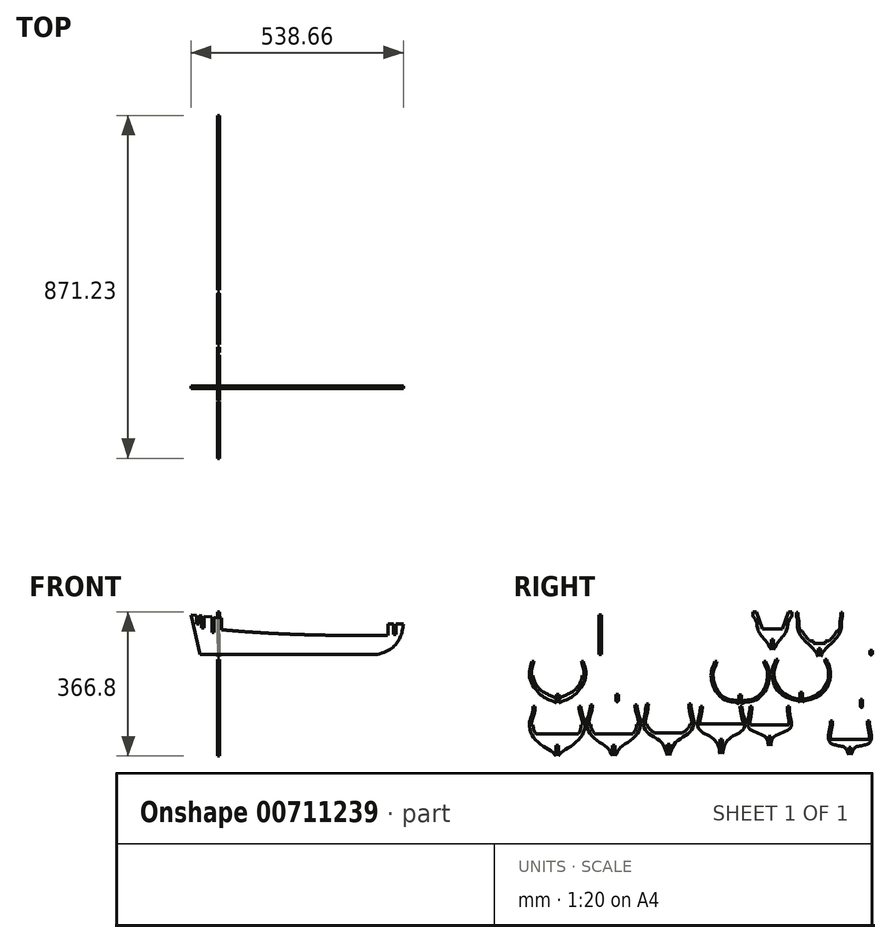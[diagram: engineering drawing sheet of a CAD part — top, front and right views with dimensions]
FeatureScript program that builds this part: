
annotation { "Feature Type Name" : "Feature", "Feature Type Description" : "" }
export const myFeature = defineFeature(function(context is Context, id is Id, definition is map)
    precondition{}
    {
        {
            var Q0;
            Q0=qCreatedBy(makeId("Right.planeOp"),FACE);
            var sketch = newSketch(context, id + "F0", { "sketchPlane" : qUnion([Q0]), "disableImprinting" : false});
            skLineSegment(sketch, "E0", {"start": v(434.23, 36.76) * mm, "end": v(434.23, -63.24) * mm, "construction": true});
            skLineSegment(sketch, "E1", {"start": v(474.96, 36.76) * mm, "end": v(484.23, 36.76) * mm, "construction": true});
            skLineSegment(sketch, "E2", {"start": v(484.23, 36.76) * mm, "end": v(484.23, 26.76) * mm});
            skFitSpline(sketch, "E3", {"points": [v(484.23, 26.76) * mm, v(475.06, 12.03) * mm, v(469.54, -13) * mm, v(437.23, -60.52) * mm], "startDerivative": vector(-48.23, -63.75) * mm, "endDerivative": vector(-86.6, -185.01) * mm});
            skLineSegment(sketch, "E4", {"start": v(431.23, -33.48) * mm, "end": v(437.23, -33.48) * mm});
            skLineSegment(sketch, "E5", {"start": v(437.23, -33.48) * mm, "end": v(437.23, -60.52) * mm});
            skLineSegment(sketch, "E6.MirrorCS", {"start": v(437.23, -33.48) * mm, "end": v(431.23, -33.48) * mm});
            skFitSpline(sketch, "E7.MirrorCS", {"points": [v(384.23, 26.76) * mm, v(393.4, 12.03) * mm, v(398.93, -13) * mm, v(431.23, -60.52) * mm], "startDerivative": vector(48.23, -63.75) * mm, "endDerivative": vector(86.6, -185.01) * mm});
            skLineSegment(sketch, "E8.MirrorCS", {"start": v(393.5, 36.76) * mm, "end": v(384.23, 36.76) * mm, "construction": true});
            skLineSegment(sketch, "E9.MirrorCS", {"start": v(384.23, 36.76) * mm, "end": v(384.23, 26.76) * mm});
            skLineSegment(sketch, "E10.MirrorCS", {"start": v(431.23, -33.48) * mm, "end": v(431.23, -60.52) * mm});
            skLineSegment(sketch, "E11", {"start": v(384.23, 36.76) * mm, "end": v(393.5, 36.76) * mm});
            skLineSegment(sketch, "E12", {"start": v(434.23, -6.45) * mm, "end": v(459.23, -6.45) * mm});
            skLineSegment(sketch, "E13", {"start": v(459.23, -6.45) * mm, "end": v(474.96, 36.76) * mm});
            skLineSegment(sketch, "E14.MirrorCS", {"start": v(409.23, -6.45) * mm, "end": v(393.5, 36.76) * mm});
            skLineSegment(sketch, "E15.MirrorCS", {"start": v(434.23, -6.45) * mm, "end": v(409.23, -6.45) * mm});
            skPoint(sketch, "E16.orphan", {"position": v(434.23, 36.76) * mm});
            skLineSegment(sketch, "E17.trimOffspring", {"start": v(474.96, 36.76) * mm, "end": v(484.23, 36.76) * mm});
            skLineSegment(sketch, "E18", {"start": v(553.88, 36.76) * mm, "end": v(553.88, -78.24) * mm, "construction": true});
            skLineSegment(sketch, "E19", {"start": v(553.88, -56.43) * mm, "end": v(556.88, -56.43) * mm});
            skLineSegment(sketch, "E20", {"start": v(556.88, -56.43) * mm, "end": v(556.88, -76.43) * mm});
            skLineSegment(sketch, "E21", {"start": v(553.88, -43.08) * mm, "end": v(568.88, -43.08) * mm});
            skLineSegment(sketch, "E22", {"start": v(568.88, -43.08) * mm, "end": v(568.88, -37.08) * mm});
            skLineSegment(sketch, "E23", {"start": v(568.88, -37.08) * mm, "end": v(577.88, -37.08) * mm});
            skFitSpline(sketch, "E24", {"points": [v(577.88, -37.08) * mm, v(597.74, -12.04) * mm], "startDerivative": vector(24.58, 23.27) * mm, "endDerivative": vector(15.3, 31.89) * mm});
            skLineSegment(sketch, "E25", {"start": v(597.74, -12.04) * mm, "end": v(602.74, -12.04) * mm});
            skFitSpline(sketch, "E26", {"points": [v(602.74, -12.04) * mm, v(605.55, -2.16) * mm, v(606.03, 9.62) * mm, v(608.04, 23.19) * mm], "startDerivative": vector(9.73, 30.2) * mm, "endDerivative": vector(10.82, 49.21) * mm});
            skLineSegment(sketch, "E27", {"start": v(608.04, 23.19) * mm, "end": v(608.04, 35.69) * mm});
            skLineSegment(sketch, "E28", {"start": v(608.04, 35.69) * mm, "end": v(612.04, 35.69) * mm});
            skLineSegment(sketch, "E29", {"start": v(612.04, 35.69) * mm, "end": v(612.04, 23.19) * mm});
            skFitSpline(sketch, "E30", {"points": [v(612.04, 23.19) * mm, v(610.08, 13.13) * mm, v(606.58, -13.87) * mm, v(581.84, -45.86) * mm, v(556.88, -76.43) * mm], "startDerivative": vector(-26.95, -57.35) * mm, "endDerivative": vector(-67.73, -147.25) * mm});
            skLineSegment(sketch, "E31.MirrorCS", {"start": v(510, -12.04) * mm, "end": v(505, -12.04) * mm});
            skLineSegment(sketch, "E32.MirrorCS", {"start": v(538.88, -43.08) * mm, "end": v(538.88, -37.08) * mm});
            skLineSegment(sketch, "E33.MirrorCS", {"start": v(499.71, 35.69) * mm, "end": v(495.71, 35.69) * mm});
            skLineSegment(sketch, "E34.MirrorCS", {"start": v(538.88, -37.08) * mm, "end": v(529.88, -37.08) * mm});
            skLineSegment(sketch, "E35.MirrorCS", {"start": v(553.88, -56.43) * mm, "end": v(550.88, -56.43) * mm});
            skLineSegment(sketch, "E36.MirrorCS", {"start": v(499.71, 23.19) * mm, "end": v(499.71, 35.69) * mm});
            skLineSegment(sketch, "E37.MirrorCS", {"start": v(553.88, -43.08) * mm, "end": v(538.88, -43.08) * mm});
            skFitSpline(sketch, "E38.MirrorCS", {"points": [v(529.88, -37.08) * mm, v(510, -12.04) * mm], "startDerivative": vector(-24.58, 23.27) * mm, "endDerivative": vector(-15.3, 31.89) * mm});
            skFitSpline(sketch, "E39.MirrorCS", {"points": [v(495.71, 23.19) * mm, v(497.67, 13.13) * mm, v(501.17, -13.87) * mm, v(525.9, -45.86) * mm, v(550.88, -76.43) * mm], "startDerivative": vector(26.95, -57.35) * mm, "endDerivative": vector(67.73, -147.25) * mm});
            skLineSegment(sketch, "E40.MirrorCS", {"start": v(495.71, 35.69) * mm, "end": v(495.71, 23.19) * mm});
            skFitSpline(sketch, "E41.MirrorCS", {"points": [v(505, -12.04) * mm, v(502.2, -2.16) * mm, v(501.73, 9.62) * mm, v(499.71, 23.19) * mm], "startDerivative": vector(-9.73, 30.2) * mm, "endDerivative": vector(-10.82, 49.21) * mm});
            skLineSegment(sketch, "E42.MirrorCS", {"start": v(550.88, -56.43) * mm, "end": v(550.88, -76.43) * mm});
            skLineSegment(sketch, "E43", {"start": v(631.29, -238.47) * mm, "end": v(631.29, -331.47) * mm, "construction": true});
            skLineSegment(sketch, "E44", {"start": v(631.29, -307.47) * mm, "end": v(634.29, -307.47) * mm});
            skLineSegment(sketch, "E45", {"start": v(634.29, -307.47) * mm, "end": v(634.29, -327.47) * mm});
            skLineSegment(sketch, "E46", {"start": v(631.29, -287.47) * mm, "end": v(680.29, -287.47) * mm});
            skFitSpline(sketch, "E47", {"points": [v(680.29, -287.47) * mm, v(676.8, -255.54) * mm, v(675.93, -240.32) * mm], "startDerivative": vector(6.96, 57.92) * mm, "endDerivative": vector(0.97, 34.08) * mm});
            skLineSegment(sketch, "E48", {"start": v(675.93, -240.32) * mm, "end": v(680.93, -240.32) * mm});
            skFitSpline(sketch, "E49.0", {"points": [v(685.26, -287.9) * mm, v(685.58, -285.19) * mm, v(685.74, -279.83) * mm, v(685.13, -273.43) * mm, v(684.4, -268.56) * mm, v(683.76, -265.07) * mm, v(683.1, -261.75) * mm, v(682.48, -258.64) * mm, v(682.02, -256.25) * mm, v(681.72, -254.48) * mm, v(681.46, -252.8) * mm, v(681.21, -250.8) * mm, v(681.02, -248.57) * mm, v(680.9, -246.45) * mm, v(680.85, -243.7) * mm, v(680.89, -241.67) * mm, v(680.93, -240.29) * mm]});
            skFitSpline(sketch, "E50", {"points": [v(685.28, -287.7) * mm, v(677.18, -298.82) * mm, v(646.16, -307.43) * mm, v(634.29, -327.47) * mm], "startDerivative": vector(-1.84, -29.1) * mm, "endDerivative": vector(-19.55, -69.03) * mm});
            skLineSegment(sketch, "E51.MirrorCS", {"start": v(631.29, -307.47) * mm, "end": v(628.29, -307.47) * mm});
            skLineSegment(sketch, "E52.MirrorCS", {"start": v(586.65, -240.32) * mm, "end": v(581.65, -240.32) * mm});
            skFitSpline(sketch, "E53.MirrorCS", {"points": [v(577.32, -287.9) * mm, v(577, -285.19) * mm, v(576.84, -279.83) * mm, v(577.44, -273.43) * mm, v(578.19, -268.56) * mm, v(578.82, -265.07) * mm, v(579.47, -261.75) * mm, v(580.1, -258.64) * mm, v(580.56, -256.25) * mm, v(580.86, -254.48) * mm, v(581.12, -252.8) * mm, v(581.36, -250.8) * mm, v(581.56, -248.57) * mm, v(581.67, -246.45) * mm, v(581.72, -243.7) * mm, v(581.69, -241.67) * mm, v(581.65, -240.29) * mm]});
            skLineSegment(sketch, "E54.MirrorCS", {"start": v(631.29, -287.47) * mm, "end": v(582.29, -287.47) * mm});
            skFitSpline(sketch, "E55.MirrorCS", {"points": [v(577.3, -287.7) * mm, v(585.4, -298.82) * mm, v(616.42, -307.43) * mm, v(628.29, -327.47) * mm], "startDerivative": vector(1.84, -29.1) * mm, "endDerivative": vector(19.55, -69.03) * mm});
            skLineSegment(sketch, "E56.MirrorCS", {"start": v(628.29, -307.47) * mm, "end": v(628.29, -327.47) * mm});
            skFitSpline(sketch, "E57.MirrorCS", {"points": [v(582.29, -287.47) * mm, v(585.78, -255.54) * mm, v(586.65, -240.32) * mm], "startDerivative": vector(-6.96, 57.92) * mm, "endDerivative": vector(-0.97, 34.08) * mm});
            skLineSegment(sketch, "E58", {"start": v(427.1, -199.94) * mm, "end": v(427.1, -292.94) * mm, "construction": true});
            skLineSegment(sketch, "E59", {"start": v(427.1, -280.2) * mm, "end": v(430.1, -280.2) * mm});
            skLineSegment(sketch, "E60", {"start": v(430.1, -280.2) * mm, "end": v(430.1, -303.67) * mm});
            skLineSegment(sketch, "E61", {"start": v(427.1, -250.2) * mm, "end": v(476.1, -250.2) * mm});
            skFitSpline(sketch, "E62", {"points": [v(476.1, -250.2) * mm, v(474.89, -230.87) * mm, v(471.92, -203.24) * mm], "startDerivative": vector(6.96, 57.92) * mm, "endDerivative": vector(0.97, 34.08) * mm});
            skLineSegment(sketch, "E63", {"start": v(471.92, -203.24) * mm, "end": v(476.92, -203.24) * mm});
            skFitSpline(sketch, "E64", {"points": [v(476.92, -203.24) * mm, v(480.45, -258.14) * mm, v(439.2, -280.1) * mm, v(430.1, -303.67) * mm], "startDerivative": vector(-10.38, -162.31) * mm, "endDerivative": vector(0, -73.72) * mm});
            skLineSegment(sketch, "E65.MirrorCS", {"start": v(382.27, -203.24) * mm, "end": v(377.27, -203.24) * mm});
            skLineSegment(sketch, "E66.MirrorCS", {"start": v(427.1, -280.2) * mm, "end": v(424.1, -280.2) * mm});
            skLineSegment(sketch, "E67.MirrorCS", {"start": v(427.1, -250.2) * mm, "end": v(378.1, -250.2) * mm});
            skFitSpline(sketch, "E68.MirrorCS", {"points": [v(378.1, -250.2) * mm, v(379.3, -230.87) * mm, v(382.27, -203.24) * mm], "startDerivative": vector(-6.96, 57.92) * mm, "endDerivative": vector(-0.97, 34.08) * mm});
            skLineSegment(sketch, "E69.MirrorCS", {"start": v(424.1, -280.2) * mm, "end": v(424.1, -303.67) * mm});
            skFitSpline(sketch, "E70.MirrorCS", {"points": [v(377.27, -203.24) * mm, v(373.73, -258.14) * mm, v(414.98, -280.1) * mm, v(424.1, -303.67) * mm], "startDerivative": vector(10.38, -162.31) * mm, "endDerivative": vector(0, -73.72) * mm});
            skLineSegment(sketch, "E71", {"start": v(304.35, -200.68) * mm, "end": v(304.35, -328.26) * mm, "construction": true});
            skLineSegment(sketch, "E72", {"start": v(304.35, -286.93) * mm, "end": v(307.35, -286.93) * mm});
            skLineSegment(sketch, "E73", {"start": v(307.35, -286.93) * mm, "end": v(307.35, -323.93) * mm});
            skFitSpline(sketch, "E74", {"points": [v(307.35, -323.93) * mm, v(322.57, -287.38) * mm, v(361.1, -261.15) * mm, v(359.82, -224.14) * mm], "startDerivative": vector(21.91, 123.1) * mm, "endDerivative": vector(-38.34, 125.11) * mm});
            skFitSpline(sketch, "E75", {"points": [v(359.82, -224.14) * mm, v(356.94, -203.59) * mm], "startDerivative": vector(-4.9, 19.8) * mm, "endDerivative": vector(-2.83, 20.59) * mm});
            skLineSegment(sketch, "E76", {"start": v(356.94, -203.59) * mm, "end": v(351.94, -203.59) * mm});
            skFitSpline(sketch, "E77", {"points": [v(351.94, -203.59) * mm, v(355.32, -226.1) * mm, v(359.16, -248.74) * mm], "startDerivative": vector(7.99, -76.81) * mm, "endDerivative": vector(-4.81, -31.55) * mm});
            skLineSegment(sketch, "E78", {"start": v(359.16, -248.74) * mm, "end": v(304.35, -248.74) * mm});
            skLineSegment(sketch, "E79.MirrorCS", {"start": v(304.35, -286.93) * mm, "end": v(301.35, -286.93) * mm});
            skLineSegment(sketch, "E80.MirrorCS", {"start": v(249.54, -248.74) * mm, "end": v(304.35, -248.74) * mm});
            skFitSpline(sketch, "E81.MirrorCS", {"points": [v(256.77, -203.59) * mm, v(253.39, -226.1) * mm, v(249.54, -248.74) * mm], "startDerivative": vector(-7.99, -76.81) * mm, "endDerivative": vector(4.81, -31.55) * mm});
            skFitSpline(sketch, "E82.MirrorCS", {"points": [v(248.89, -224.14) * mm, v(251.77, -203.59) * mm], "startDerivative": vector(4.9, 19.8) * mm, "endDerivative": vector(2.83, 20.59) * mm});
            skLineSegment(sketch, "E83.MirrorCS", {"start": v(251.77, -203.59) * mm, "end": v(256.77, -203.59) * mm});
            skLineSegment(sketch, "E84.MirrorCS", {"start": v(301.35, -286.93) * mm, "end": v(301.35, -323.93) * mm});
            skFitSpline(sketch, "E85.MirrorCS", {"points": [v(301.35, -323.93) * mm, v(286.14, -287.38) * mm, v(247.6, -261.15) * mm, v(248.89, -224.14) * mm], "startDerivative": vector(-21.91, 123.1) * mm, "endDerivative": vector(38.34, 125.11) * mm});
            skLineSegment(sketch, "E86", {"start": v(170.41, -197.14) * mm, "end": v(170.41, -329.52) * mm, "construction": true});
            skLineSegment(sketch, "E87", {"start": v(170.41, -300.4) * mm, "end": v(173.41, -300.4) * mm});
            skLineSegment(sketch, "E88", {"start": v(173.41, -300.4) * mm, "end": v(173.41, -327.9) * mm});
            skFitSpline(sketch, "E89", {"points": [v(173.41, -327.9) * mm, v(188.1, -295.59) * mm, v(221.3, -271.7) * mm, v(234.8, -248.5) * mm, v(231.3, -227.53) * mm, v(226.84, -197.94) * mm], "startDerivative": vector(45.22, 164.82) * mm, "endDerivative": vector(-18.15, 163.37) * mm});
            skLineSegment(sketch, "E90", {"start": v(226.84, -197.94) * mm, "end": v(221.84, -197.94) * mm});
            skFitSpline(sketch, "E91", {"points": [v(221.84, -197.94) * mm, v(224.92, -222.59) * mm, v(229.57, -245.81) * mm, v(223.41, -262.16) * mm], "startDerivative": vector(5.07, -69.05) * mm, "endDerivative": vector(-26.5, -52.4) * mm});
            skLineSegment(sketch, "E92", {"start": v(205.06, -271.4) * mm, "end": v(170.41, -271.4) * mm});
            skLineSegment(sketch, "E93", {"start": v(229.37, -247.6) * mm, "end": v(225.37, -247.6) * mm});
            skFitSpline(sketch, "E94", {"points": [v(225.37, -247.6) * mm, v(205.06, -271.4) * mm], "startDerivative": vector(-6.96, -33.33) * mm, "endDerivative": vector(-27.82, -17.37) * mm});
            skPoint(sketch, "E95.MirrorCS.end.orphan", {"position": v(170.41, -271.4) * mm});
            skLineSegment(sketch, "E96.MirrorCS", {"start": v(113.98, -197.94) * mm, "end": v(118.98, -197.94) * mm});
            skLineSegment(sketch, "E97.MirrorCS", {"start": v(111.46, -247.6) * mm, "end": v(115.46, -247.6) * mm});
            skFitSpline(sketch, "E98.MirrorCS", {"points": [v(115.46, -247.6) * mm, v(135.76, -271.4) * mm], "startDerivative": vector(6.96, -33.33) * mm, "endDerivative": vector(27.82, -17.37) * mm});
            skLineSegment(sketch, "E99.MirrorCS", {"start": v(170.41, -300.4) * mm, "end": v(167.41, -300.4) * mm});
            skLineSegment(sketch, "E100.MirrorCS", {"start": v(167.41, -300.4) * mm, "end": v(167.41, -327.9) * mm});
            skFitSpline(sketch, "E101.MirrorCS", {"points": [v(167.41, -327.9) * mm, v(152.72, -295.59) * mm, v(119.52, -271.7) * mm, v(106.03, -248.5) * mm, v(109.53, -227.53) * mm, v(113.98, -197.94) * mm], "startDerivative": vector(-45.22, 164.82) * mm, "endDerivative": vector(18.15, 163.37) * mm});
            skFitSpline(sketch, "E102.MirrorCS", {"points": [v(118.98, -197.94) * mm, v(115.9, -222.59) * mm, v(111.26, -245.81) * mm, v(117.41, -262.16) * mm], "startDerivative": vector(-5.07, -69.05) * mm, "endDerivative": vector(26.5, -52.4) * mm});
            skLineSegment(sketch, "E103.MirrorCS", {"start": v(135.76, -271.4) * mm, "end": v(170.41, -271.4) * mm});
            skLineSegment(sketch, "E104", {"start": v(31.21, -330.55) * mm, "end": v(31.21, -197.66) * mm, "construction": true});
            skLineSegment(sketch, "E105", {"start": v(31.21, -302.26) * mm, "end": v(34.21, -302.26) * mm});
            skLineSegment(sketch, "E106", {"start": v(34.21, -302.26) * mm, "end": v(34.21, -329.26) * mm});
            skLineSegment(sketch, "E107", {"start": v(31.21, -273.26) * mm, "end": v(79.56, -273.26) * mm});
            skFitSpline(sketch, "E108", {"points": [v(79.56, -273.26) * mm, v(89.54, -249.8) * mm], "startDerivative": vector(14.49, 20.05) * mm, "endDerivative": vector(2.55, 34.74) * mm});
            skLineSegment(sketch, "E109", {"start": v(89.54, -249.8) * mm, "end": v(94, -249.8) * mm});
            skFitSpline(sketch, "E110", {"points": [v(34.21, -329.26) * mm, v(50.47, -306.43) * mm, v(86.42, -278.69) * mm, v(99.58, -243.24) * mm, v(94.07, -222.41) * mm, v(90.4, -200.06) * mm], "startDerivative": vector(65.96, 123.7) * mm, "endDerivative": vector(4.47, 119.64) * mm});
            skLineSegment(sketch, "E111", {"start": v(90.4, -200.06) * mm, "end": v(85.4, -200.06) * mm});
            skFitSpline(sketch, "E112", {"points": [v(85.4, -200.06) * mm, v(89.3, -224.07) * mm, v(94, -249.8) * mm], "startDerivative": vector(-0.26, -49.5) * mm, "endDerivative": vector(-5.6, -59.38) * mm});
            skLineSegment(sketch, "E113.MirrorCS", {"start": v(31.21, -302.26) * mm, "end": v(28.21, -302.26) * mm});
            skLineSegment(sketch, "E114.MirrorCS", {"start": v(-27.12, -249.8) * mm, "end": v(-31.58, -249.8) * mm});
            skLineSegment(sketch, "E115.MirrorCS", {"start": v(-27.98, -200.06) * mm, "end": v(-22.98, -200.06) * mm});
            skFitSpline(sketch, "E116.MirrorCS", {"points": [v(-17.14, -273.26) * mm, v(-27.12, -249.8) * mm], "startDerivative": vector(-14.49, 20.05) * mm, "endDerivative": vector(-2.55, 34.74) * mm});
            skFitSpline(sketch, "E117.MirrorCS", {"points": [v(-22.98, -200.06) * mm, v(-26.88, -224.07) * mm, v(-31.58, -249.8) * mm], "startDerivative": vector(0.26, -49.5) * mm, "endDerivative": vector(5.6, -59.38) * mm});
            skLineSegment(sketch, "E118.MirrorCS", {"start": v(28.21, -302.26) * mm, "end": v(28.21, -329.26) * mm});
            skFitSpline(sketch, "E119.MirrorCS", {"points": [v(28.21, -329.26) * mm, v(11.96, -306.43) * mm, v(-24, -278.69) * mm, v(-37.16, -243.24) * mm, v(-31.65, -222.41) * mm, v(-27.98, -200.06) * mm], "startDerivative": vector(-65.96, 123.7) * mm, "endDerivative": vector(-4.47, 119.64) * mm});
            skLineSegment(sketch, "E120.MirrorCS", {"start": v(31.21, -273.26) * mm, "end": v(-17.14, -273.26) * mm});
            skLineSegment(sketch, "E121", {"start": v(-112.69, -331.84) * mm, "end": v(-112.69, -198.94) * mm, "construction": true});
            skLineSegment(sketch, "E122", {"start": v(-112.69, -303.04) * mm, "end": v(-109.69, -303.04) * mm});
            skLineSegment(sketch, "E123", {"start": v(-109.69, -303.04) * mm, "end": v(-109.69, -330.04) * mm});
            skLineSegment(sketch, "E124", {"start": v(-112.69, -274.04) * mm, "end": v(-59.17, -274.04) * mm});
            skFitSpline(sketch, "E125", {"points": [v(-59.17, -274.04) * mm, v(-51.62, -250.77) * mm], "startDerivative": vector(14.49, 20.05) * mm, "endDerivative": vector(2.55, 34.74) * mm});
            skLineSegment(sketch, "E126", {"start": v(-51.62, -250.77) * mm, "end": v(-47.62, -250.77) * mm});
            skFitSpline(sketch, "E127", {"points": [v(-109.69, -330.04) * mm, v(-88.39, -311.83) * mm, v(-52, -281.07) * mm, v(-42.34, -248.14) * mm, v(-48.65, -223.57) * mm, v(-52.03, -203.28) * mm], "startDerivative": vector(65.96, 123.7) * mm, "endDerivative": vector(4.47, 119.64) * mm});
            skLineSegment(sketch, "E128", {"start": v(-52.03, -203.28) * mm, "end": v(-57.03, -203.28) * mm});
            skFitSpline(sketch, "E129", {"points": [v(-57.03, -203.28) * mm, v(-53.27, -226.4) * mm, v(-47.62, -250.77) * mm], "startDerivative": vector(-0.26, -49.5) * mm, "endDerivative": vector(-1.18, -57.37) * mm});
            skLineSegment(sketch, "E130.MirrorCS", {"start": v(-173.35, -203.28) * mm, "end": v(-168.35, -203.28) * mm});
            skLineSegment(sketch, "E131.MirrorCS", {"start": v(-112.69, -303.04) * mm, "end": v(-115.69, -303.04) * mm});
            skLineSegment(sketch, "E132.MirrorCS", {"start": v(-173.76, -250.77) * mm, "end": v(-177.76, -250.77) * mm});
            skFitSpline(sketch, "E133.MirrorCS", {"points": [v(-166.21, -274.04) * mm, v(-173.76, -250.77) * mm], "startDerivative": vector(-14.49, 20.05) * mm, "endDerivative": vector(-2.55, 34.74) * mm});
            skFitSpline(sketch, "E134.MirrorCS", {"points": [v(-115.69, -330.04) * mm, v(-136.99, -311.83) * mm, v(-173.37, -281.07) * mm, v(-183.04, -248.14) * mm, v(-176.73, -223.57) * mm, v(-173.35, -203.28) * mm], "startDerivative": vector(-65.96, 123.7) * mm, "endDerivative": vector(-4.47, 119.64) * mm});
            skFitSpline(sketch, "E135.MirrorCS", {"points": [v(-168.35, -203.28) * mm, v(-172.1, -226.4) * mm, v(-177.76, -250.77) * mm], "startDerivative": vector(0.26, -49.5) * mm, "endDerivative": vector(1.18, -57.37) * mm});
            skLineSegment(sketch, "E136.MirrorCS", {"start": v(-115.69, -303.04) * mm, "end": v(-115.69, -330.04) * mm});
            skLineSegment(sketch, "E137.MirrorCS", {"start": v(-112.69, -274.04) * mm, "end": v(-166.21, -274.04) * mm});
            skLineSegment(sketch, "E138", {"start": v(660.6, -86.17) * mm, "end": v(660.6, -218.2) * mm, "construction": true});
            skLineSegment(sketch, "E139", {"start": v(660.6, -186.45) * mm, "end": v(663.6, -186.45) * mm});
            skLineSegment(sketch, "E140", {"start": v(660.6, -158.45) * mm, "end": v(719.89, -158.45) * mm});
            skLineSegment(sketch, "E141", {"start": v(663.6, -186.45) * mm, "end": v(663.6, -212.64) * mm});
            skFitSpline(sketch, "E142", {"points": [v(663.6, -212.64) * mm, v(683.93, -201.2) * mm, v(715.46, -181.17) * mm, v(733.68, -139.31) * mm, v(726.03, -107.08) * mm, v(723.1, -87.44) * mm], "startDerivative": vector(105.46, 87.45) * mm, "endDerivative": vector(0, 69.3) * mm});
            skLineSegment(sketch, "E143", {"start": v(723.1, -87.44) * mm, "end": v(718.1, -87.44) * mm});
            skLineSegment(sketch, "E144", {"start": v(724.52, -135.14) * mm, "end": v(728.52, -135.14) * mm});
            skPoint(sketch, "E145", {"position": v(728.52, -135.14) * mm});
            skFitSpline(sketch, "E146.trimOffspring", {"points": [v(657.89, -205.7) * mm, v(659.19, -204.63) * mm, v(661.82, -202.64) * mm, v(665.83, -200.08) * mm, v(669.88, -197.86) * mm, v(673.96, -195.85) * mm, v(677.41, -194.27) * mm, v(680.23, -193) * mm, v(683.09, -191.71) * mm, v(686.7, -190.05) * mm, v(691.07, -187.9) * mm, v(695.38, -185.53) * mm, v(699.57, -182.91) * mm, v(703.57, -180) * mm, v(706.7, -177.26) * mm, v(709.06, -174.89) * mm, v(710.77, -172.98) * mm, v(712.43, -170.93) * mm, v(714.55, -168.05) * mm, v(717.02, -164.2) * mm, v(719.58, -159.3) * mm, v(721.7, -154.26) * mm, v(723.3, -149.24) * mm, v(724.16, -145.19) * mm, v(724.56, -142.1) * mm, v(724.71, -139.89) * mm, v(724.72, -137.8) * mm, v(724.6, -135.71) * mm, v(724.34, -133.64) * mm, v(723.86, -130.85) * mm, v(722.99, -127.3) * mm, v(721.85, -123.6) * mm, v(720.83, -120.54) * mm, v(720.04, -118.17) * mm, v(719.23, -115.73) * mm, v(718.43, -113.2) * mm, v(717.67, -110.59) * mm, v(716.97, -107.88) * mm, v(716.37, -105.2) * mm, v(715.68, -101.68) * mm, v(715.03, -97.46) * mm, v(714.51, -92.89) * mm, v(714.22, -88.98) * mm, v(714.14, -86.94) * mm, v(714.12, -86.06) * mm]});
            skFitSpline(sketch, "E147.trimOffspring", {"points": [v(660.28, -207.29) * mm, v(662.7, -205.28) * mm, v(666.42, -202.73) * mm, v(671.56, -199.92) * mm, v(675.5, -197.98) * mm, v(678.9, -196.42) * mm, v(681.71, -195.16) * mm, v(684.58, -193.86) * mm, v(688.26, -192.17) * mm, v(692.75, -189.96) * mm, v(697.24, -187.5) * mm, v(701.65, -184.75) * mm, v(705.91, -181.64) * mm, v(709.28, -178.72) * mm, v(711.83, -176.15) * mm, v(713.67, -174.09) * mm, v(715.45, -171.9) * mm, v(717.72, -168.82) * mm, v(720.33, -164.72) * mm, v(723.06, -159.53) * mm, v(725.3, -154.18) * mm, v(727.02, -148.8) * mm, v(727.96, -144.41) * mm, v(728.4, -141.02) * mm, v(728.57, -138.56) * mm, v(728.59, -136.2) * mm, v(728.45, -133.87) * mm, v(728.17, -131.57) * mm, v(727.64, -128.52) * mm, v(726.72, -124.73) * mm, v(725.3, -120.14) * mm, v(723.98, -116.23) * mm, v(722.92, -113.02) * mm, v(722.14, -110.56) * mm, v(721.4, -108.05) * mm, v(720.73, -105.48) * mm, v(720.15, -102.91) * mm, v(719.49, -99.54) * mm, v(718.85, -95.47) * mm, v(718.34, -91.03) * mm, v(718.1, -87.87) * mm, v(718.02, -85.76) * mm, v(718, -84.85) * mm, v(718, -84.42) * mm]});
            skLineSegment(sketch, "E148", {"start": v(728.52, -135.14) * mm, "end": v(728.52, -135.14) * mm});
            skLineSegment(sketch, "E149", {"start": v(507.81, -69.62) * mm, "end": v(507.81, -203.28) * mm, "construction": true});
            skLineSegment(sketch, "E150", {"start": v(507.81, -167.59) * mm, "end": v(510.81, -167.59) * mm});
            skLineSegment(sketch, "E151", {"start": v(522.81, -141.59) * mm, "end": v(568.66, -141.59) * mm});
            skLineSegment(sketch, "E152", {"start": v(510.81, -167.59) * mm, "end": v(510.81, -193.19) * mm});
            skFitSpline(sketch, "E153", {"points": [v(510.81, -193.19) * mm, v(532.9, -185.75) * mm, v(565.02, -166.24) * mm, v(581.24, -131.9) * mm, v(578.8, -101.51) * mm, v(572.64, -83.99) * mm], "startDerivative": vector(105.46, 87.45) * mm, "endDerivative": vector(0, 69.3) * mm});
            skLineSegment(sketch, "E154", {"start": v(572.64, -83.99) * mm, "end": v(567.64, -83.99) * mm});
            skLineSegment(sketch, "E155", {"start": v(572.99, -117.3) * mm, "end": v(576.99, -117.3) * mm});
            skPoint(sketch, "E156", {"position": v(576.99, -117.3) * mm});
            skFitSpline(sketch, "E157.trimOffspring", {"points": [v(506.52, -189.15) * mm, v(507.82, -188.07) * mm, v(510.45, -186.08) * mm, v(514.47, -183.53) * mm, v(518.52, -181.3) * mm, v(522.6, -179.3) * mm, v(526.05, -177.72) * mm, v(528.86, -176.45) * mm, v(531.72, -175.16) * mm, v(535.34, -173.5) * mm, v(539.7, -171.34) * mm, v(544.01, -168.97) * mm, v(548.2, -166.35) * mm, v(552.2, -163.44) * mm, v(555.34, -160.7) * mm, v(557.7, -158.33) * mm, v(559.4, -156.42) * mm, v(561.07, -154.37) * mm, v(563.19, -151.5) * mm, v(565.65, -147.64) * mm, v(568.22, -142.74) * mm, v(570.33, -137.7) * mm, v(571.93, -132.68) * mm, v(572.8, -128.63) * mm, v(573.2, -125.55) * mm, v(573.35, -123.33) * mm, v(573.35, -121.24) * mm, v(573.23, -119.16) * mm, v(572.98, -117.08) * mm, v(572.5, -114.3) * mm, v(571.62, -110.75) * mm, v(570.48, -107.05) * mm, v(569.46, -103.98) * mm, v(568.67, -101.61) * mm, v(567.86, -99.17) * mm, v(567.07, -96.65) * mm, v(566.3, -94.03) * mm, v(565.6, -91.32) * mm, v(565, -88.64) * mm, v(564.32, -85.12) * mm, v(563.66, -80.9) * mm, v(563.15, -76.33) * mm, v(562.85, -72.42) * mm, v(562.77, -70.38) * mm, v(562.76, -69.5) * mm]});
            skFitSpline(sketch, "E158.trimOffspring", {"points": [v(507.62, -189.34) * mm, v(509, -188.2) * mm, v(511.85, -186.33) * mm, v(516.22, -184.53) * mm, v(520.49, -183.39) * mm, v(523.92, -182.7) * mm, v(526.6, -182.16) * mm, v(528.59, -181.73) * mm, v(530.55, -181.24) * mm, v(532.5, -180.66) * mm, v(534.5, -179.97) * mm, v(537.24, -178.9) * mm, v(540.74, -177.27) * mm, v(544.97, -174.93) * mm, v(549.15, -172.2) * mm, v(553.22, -169.15) * mm, v(557.08, -165.8) * mm, v(560.07, -162.79) * mm, v(562.29, -160.27) * mm, v(564.4, -157.68) * mm, v(566.84, -154.3) * mm, v(570.29, -148.7) * mm, v(573.71, -141.36) * mm, v(575.89, -133.86) * mm, v(576.84, -127.95) * mm, v(577.17, -123.54) * mm, v(577.16, -119.18) * mm, v(576.8, -114.89) * mm, v(576.25, -111.38) * mm, v(575.66, -108.63) * mm, v(575.14, -106.6) * mm, v(574.65, -104.93) * mm, v(574.23, -103.6) * mm, v(573.79, -102.3) * mm, v(573.18, -100.67) * mm, v(572.16, -98.07) * mm, v(570.81, -94.9) * mm, v(569.56, -91.86) * mm, v(568.7, -89.5) * mm, v(568.17, -87.75) * mm, v(567.77, -85.96) * mm, v(567.64, -84.67) * mm, v(567.64, -83.99) * mm]});
            skLineSegment(sketch, "E159", {"start": v(576.99, -117.3) * mm, "end": v(576.99, -117.3) * mm});
            skLineSegment(sketch, "E160.MirrorCS", {"start": v(596.7, -135.14) * mm, "end": v(592.7, -135.14) * mm});
            skLineSegment(sketch, "E161.MirrorCS", {"start": v(660.6, -186.45) * mm, "end": v(657.6, -186.45) * mm});
            skLineSegment(sketch, "E162.MirrorCS", {"start": v(598.12, -87.44) * mm, "end": v(603.12, -87.44) * mm});
            skPoint(sketch, "E163.MirrorP", {"position": v(592.7, -135.14) * mm});
            skLineSegment(sketch, "E164.MirrorCS", {"start": v(660.6, -158.45) * mm, "end": v(601.33, -158.45) * mm});
            skLineSegment(sketch, "E165.MirrorCS", {"start": v(657.6, -186.45) * mm, "end": v(657.6, -212.64) * mm});
            skFitSpline(sketch, "E166.MirrorCS", {"points": [v(657.6, -212.64) * mm, v(637.29, -201.2) * mm, v(605.76, -181.17) * mm, v(587.53, -139.31) * mm, v(595.18, -107.08) * mm, v(598.12, -87.44) * mm], "startDerivative": vector(-105.46, 87.45) * mm, "endDerivative": vector(0, 69.3) * mm});
            skLineSegment(sketch, "E167.MirrorCS", {"start": v(592.7, -135.14) * mm, "end": v(592.7, -135.14) * mm});
            skFitSpline(sketch, "E168.MirrorCS", {"points": [v(660.94, -207.29) * mm, v(658.52, -205.28) * mm, v(654.8, -202.73) * mm, v(649.66, -199.92) * mm, v(645.71, -197.98) * mm, v(642.31, -196.42) * mm, v(639.5, -195.16) * mm, v(636.63, -193.86) * mm, v(632.95, -192.17) * mm, v(628.46, -189.96) * mm, v(623.98, -187.5) * mm, v(619.57, -184.75) * mm, v(615.3, -181.64) * mm, v(611.94, -178.72) * mm, v(609.4, -176.15) * mm, v(607.55, -174.09) * mm, v(605.77, -171.9) * mm, v(603.5, -168.82) * mm, v(600.89, -164.72) * mm, v(598.16, -159.53) * mm, v(595.91, -154.18) * mm, v(594.2, -148.8) * mm, v(593.26, -144.41) * mm, v(592.82, -141.02) * mm, v(592.64, -138.56) * mm, v(592.63, -136.2) * mm, v(592.77, -133.87) * mm, v(593.05, -131.57) * mm, v(593.57, -128.52) * mm, v(594.5, -124.73) * mm, v(595.92, -120.14) * mm, v(597.24, -116.23) * mm, v(598.3, -113.02) * mm, v(599.08, -110.56) * mm, v(599.81, -108.05) * mm, v(600.49, -105.48) * mm, v(601.06, -102.91) * mm, v(601.73, -99.54) * mm, v(602.37, -95.47) * mm, v(602.88, -91.03) * mm, v(603.1, -87.87) * mm, v(603.2, -85.76) * mm, v(603.21, -84.85) * mm, v(603.21, -84.42) * mm]});
            skFitSpline(sketch, "E169.MirrorCS", {"points": [v(663.33, -205.7) * mm, v(662.03, -204.63) * mm, v(659.4, -202.64) * mm, v(655.38, -200.08) * mm, v(651.33, -197.86) * mm, v(647.25, -195.85) * mm, v(643.8, -194.27) * mm, v(640.99, -193) * mm, v(638.13, -191.71) * mm, v(634.51, -190.05) * mm, v(630.15, -187.9) * mm, v(625.84, -185.53) * mm, v(621.65, -182.91) * mm, v(617.64, -180) * mm, v(614.5, -177.26) * mm, v(612.15, -174.89) * mm, v(610.44, -172.98) * mm, v(608.78, -170.93) * mm, v(606.66, -168.05) * mm, v(604.2, -164.2) * mm, v(601.63, -159.3) * mm, v(599.52, -154.26) * mm, v(597.92, -149.24) * mm, v(597.06, -145.19) * mm, v(596.66, -142.1) * mm, v(596.5, -139.89) * mm, v(596.5, -137.8) * mm, v(596.62, -135.71) * mm, v(596.87, -133.64) * mm, v(597.36, -130.85) * mm, v(598.23, -127.3) * mm, v(599.37, -123.6) * mm, v(600.39, -120.54) * mm, v(601.18, -118.17) * mm, v(601.99, -115.73) * mm, v(602.78, -113.2) * mm, v(603.55, -110.59) * mm, v(604.25, -107.88) * mm, v(604.85, -105.2) * mm, v(605.53, -101.68) * mm, v(606.19, -97.46) * mm, v(606.7, -92.89) * mm, v(607, -88.98) * mm, v(607.08, -86.94) * mm, v(607.1, -86.06) * mm]});
            skLineSegment(sketch, "E170", {"start": v(606.26, -201.43) * mm, "end": v(606.26, -201.43) * mm});
            skLineSegment(sketch, "E171", {"start": v(352.85, -71.56) * mm, "end": v(352.85, -197.83) * mm, "construction": true});
            skLineSegment(sketch, "E172", {"start": v(352.85, -174.23) * mm, "end": v(355.85, -174.23) * mm});
            skLineSegment(sketch, "E173", {"start": v(352.85, -148.23) * mm, "end": v(412.48, -148.23) * mm});
            skLineSegment(sketch, "E174", {"start": v(355.85, -174.23) * mm, "end": v(355.85, -196.99) * mm});
            skFitSpline(sketch, "E175", {"points": [v(355.85, -196.99) * mm, v(383.56, -190.18) * mm, v(414.33, -167.23) * mm, v(426.7, -129.68) * mm, v(424.26, -106.62) * mm, v(417.56, -88.81) * mm], "startDerivative": vector(203.97, 94.33) * mm, "endDerivative": vector(0, 69.3) * mm});
            skLineSegment(sketch, "E176", {"start": v(417.56, -88.81) * mm, "end": v(412.56, -88.81) * mm});
            skLineSegment(sketch, "E177", {"start": v(418.01, -121.87) * mm, "end": v(422.01, -121.87) * mm});
            skPoint(sketch, "E178", {"position": v(422.01, -121.87) * mm});
            skFitSpline(sketch, "E179.trimOffspring", {"points": [v(351.5, -193.36) * mm, v(352.8, -192.29) * mm, v(355.43, -190.3) * mm, v(359.44, -187.74) * mm, v(363.49, -185.51) * mm, v(367.57, -183.51) * mm, v(371.02, -181.93) * mm, v(373.84, -180.66) * mm, v(376.7, -179.37) * mm, v(380.31, -177.7) * mm, v(384.68, -175.55) * mm, v(388.99, -173.19) * mm, v(393.18, -170.57) * mm, v(397.18, -167.65) * mm, v(400.31, -164.92) * mm, v(402.67, -162.55) * mm, v(404.38, -160.63) * mm, v(406.04, -158.59) * mm, v(408.16, -155.7) * mm, v(410.62, -151.85) * mm, v(413.19, -146.95) * mm, v(415.3, -141.92) * mm, v(416.9, -136.9) * mm, v(417.77, -132.84) * mm, v(418.17, -129.76) * mm, v(418.32, -127.55) * mm, v(418.33, -125.45) * mm, v(418.2, -123.37) * mm, v(417.95, -121.3) * mm, v(417.46, -118.5) * mm, v(416.6, -114.96) * mm, v(415.45, -111.27) * mm, v(414.44, -108.2) * mm, v(413.64, -105.83) * mm, v(412.84, -103.38) * mm, v(412.04, -100.86) * mm, v(411.27, -98.25) * mm, v(410.57, -95.53) * mm, v(409.97, -92.85) * mm, v(409.3, -89.34) * mm, v(408.64, -85.12) * mm, v(408.12, -80.54) * mm, v(407.82, -76.64) * mm, v(407.74, -74.6) * mm, v(407.73, -73.72) * mm]});
            skFitSpline(sketch, "E180.trimOffspring", {"points": [v(353.75, -192.45) * mm, v(356.02, -191.4) * mm, v(360.24, -189.71) * mm, v(365.77, -188.16) * mm, v(370.6, -187.32) * mm, v(374.78, -186.87) * mm, v(377.8, -186.56) * mm, v(380.04, -186.22) * mm, v(381.42, -185.94) * mm, v(382.52, -185.67) * mm, v(383.64, -185.35) * mm, v(385.1, -184.86) * mm, v(386.97, -184.11) * mm, v(388.9, -183.21) * mm, v(390.9, -182.17) * mm, v(393.6, -180.6) * mm, v(397, -178.3) * mm, v(401.02, -175.07) * mm, v(404.2, -172.04) * mm, v(406.57, -169.45) * mm, v(408.26, -167.43) * mm, v(409.84, -165.34) * mm, v(411.77, -162.48) * mm, v(413.92, -158.7) * mm, v(416.09, -153.95) * mm, v(417.87, -149.04) * mm, v(419.29, -144.09) * mm, v(420.38, -139.16) * mm, v(421.04, -135.17) * mm, v(421.43, -132.09) * mm, v(421.67, -129.84) * mm, v(421.85, -127.68) * mm, v(422, -124.93) * mm, v(422.05, -121.71) * mm, v(421.84, -118.11) * mm, v(421.44, -115.25) * mm, v(420.95, -112.97) * mm, v(420.51, -111.25) * mm, v(419.98, -109.52) * mm, v(419.15, -107.16) * mm, v(417.84, -104.01) * mm, v(416.1, -100.15) * mm, v(414.71, -97) * mm, v(413.77, -94.55) * mm, v(413.17, -92.73) * mm, v(412.71, -90.88) * mm, v(412.56, -89.54) * mm, v(412.56, -88.81) * mm]});
            skLineSegment(sketch, "E181", {"start": v(522.81, -141.59) * mm, "end": v(522.81, -148.59) * mm});
            skLineSegment(sketch, "E182", {"start": v(522.81, -148.59) * mm, "end": v(507.81, -148.59) * mm});
            skPoint(sketch, "E183.orphan", {"position": v(507.81, -141.59) * mm});
            skLineSegment(sketch, "E184.MirrorCS", {"start": v(442.64, -117.3) * mm, "end": v(438.64, -117.3) * mm});
            skLineSegment(sketch, "E185.MirrorCS", {"start": v(443, -83.99) * mm, "end": v(448, -83.99) * mm});
            skPoint(sketch, "E186.MirrorP", {"position": v(438.64, -117.3) * mm});
            skLineSegment(sketch, "E187.MirrorCS", {"start": v(492.81, -148.59) * mm, "end": v(507.81, -148.59) * mm});
            skLineSegment(sketch, "E188.MirrorCS", {"start": v(507.81, -167.59) * mm, "end": v(504.81, -167.59) * mm});
            skLineSegment(sketch, "E189.MirrorCS", {"start": v(492.81, -141.59) * mm, "end": v(492.81, -148.59) * mm});
            skLineSegment(sketch, "E190.MirrorCS", {"start": v(504.81, -167.59) * mm, "end": v(504.81, -193.19) * mm});
            skLineSegment(sketch, "E191.MirrorCS", {"start": v(492.81, -141.59) * mm, "end": v(446.97, -141.59) * mm});
            skFitSpline(sketch, "E192.MirrorCS", {"points": [v(509.1, -189.15) * mm, v(507.8, -188.07) * mm, v(505.17, -186.08) * mm, v(501.16, -183.53) * mm, v(497.11, -181.3) * mm, v(493.03, -179.3) * mm, v(489.58, -177.72) * mm, v(486.77, -176.45) * mm, v(483.9, -175.16) * mm, v(480.29, -173.5) * mm, v(475.93, -171.34) * mm, v(471.61, -168.97) * mm, v(467.42, -166.35) * mm, v(463.42, -163.44) * mm, v(460.29, -160.7) * mm, v(457.93, -158.33) * mm, v(456.22, -156.42) * mm, v(454.56, -154.37) * mm, v(452.44, -151.5) * mm, v(449.98, -147.64) * mm, v(447.41, -142.74) * mm, v(445.3, -137.7) * mm, v(443.7, -132.68) * mm, v(442.84, -128.63) * mm, v(442.44, -125.55) * mm, v(442.28, -123.33) * mm, v(442.28, -121.24) * mm, v(442.4, -119.16) * mm, v(442.65, -117.08) * mm, v(443.14, -114.3) * mm, v(444, -110.75) * mm, v(445.15, -107.05) * mm, v(446.16, -103.98) * mm, v(446.96, -101.61) * mm, v(447.77, -99.17) * mm, v(448.56, -96.65) * mm, v(449.33, -94.03) * mm, v(450.03, -91.32) * mm, v(450.63, -88.64) * mm, v(451.31, -85.12) * mm, v(451.96, -80.9) * mm, v(452.48, -76.33) * mm, v(452.78, -72.42) * mm, v(452.86, -70.38) * mm, v(452.87, -69.5) * mm]});
            skFitSpline(sketch, "E193.MirrorCS", {"points": [v(508, -189.34) * mm, v(506.64, -188.2) * mm, v(503.78, -186.33) * mm, v(499.41, -184.53) * mm, v(495.14, -183.39) * mm, v(491.7, -182.7) * mm, v(489.03, -182.16) * mm, v(487.04, -181.73) * mm, v(485.08, -181.24) * mm, v(483.13, -180.66) * mm, v(481.12, -179.97) * mm, v(478.39, -178.9) * mm, v(474.9, -177.27) * mm, v(470.66, -174.93) * mm, v(466.48, -172.2) * mm, v(462.41, -169.15) * mm, v(458.55, -165.8) * mm, v(455.56, -162.79) * mm, v(453.34, -160.27) * mm, v(451.22, -157.68) * mm, v(448.79, -154.3) * mm, v(445.34, -148.7) * mm, v(441.92, -141.36) * mm, v(439.74, -133.86) * mm, v(438.8, -127.95) * mm, v(438.45, -123.54) * mm, v(438.47, -119.18) * mm, v(438.82, -114.89) * mm, v(439.38, -111.38) * mm, v(439.97, -108.63) * mm, v(440.49, -106.6) * mm, v(440.97, -104.93) * mm, v(441.4, -103.6) * mm, v(441.84, -102.3) * mm, v(442.44, -100.67) * mm, v(443.47, -98.07) * mm, v(444.81, -94.9) * mm, v(446.07, -91.86) * mm, v(446.92, -89.5) * mm, v(447.46, -87.75) * mm, v(447.86, -85.96) * mm, v(448, -84.67) * mm, v(448, -83.99) * mm]});
            skLineSegment(sketch, "E194.MirrorCS", {"start": v(438.64, -117.3) * mm, "end": v(438.64, -117.3) * mm});
            skFitSpline(sketch, "E195.MirrorCS", {"points": [v(504.81, -193.19) * mm, v(482.72, -185.75) * mm, v(450.6, -166.24) * mm, v(434.39, -131.9) * mm, v(436.83, -101.51) * mm, v(443, -83.99) * mm], "startDerivative": vector(-105.46, 87.45) * mm, "endDerivative": vector(0, 69.3) * mm});
            skLineSegment(sketch, "E196", {"start": v(684.79, 49.16) * mm, "end": v(684.79, -84.42) * mm, "construction": true});
            skLineSegment(sketch, "E197", {"start": v(684.79, -61.42) * mm, "end": v(687.79, -61.42) * mm});
            skLineSegment(sketch, "E198", {"start": v(687.79, -61.42) * mm, "end": v(687.79, -82.2) * mm});
            skLineSegment(sketch, "E199", {"start": v(684.79, -36.92) * mm, "end": v(729.56, -36.92) * mm});
            skFitSpline(sketch, "E200", {"points": [v(687.79, -82.2) * mm, v(717.58, -60.3) * mm, v(746.76, -27.7) * mm, v(751.56, 2.85) * mm, v(748.15, 32) * mm], "startDerivative": vector(112.56, 79.93) * mm, "endDerivative": vector(4.41, 198.36) * mm});
            skLineSegment(sketch, "E201", {"start": v(748.15, 32) * mm, "end": v(743.15, 32) * mm});
            skFitSpline(sketch, "E202.trimOffspring", {"points": [v(684.91, -78.02) * mm, v(689.63, -74.68) * mm, v(696.72, -69.73) * mm, v(706.36, -62.66) * mm, v(713.71, -56.96) * mm, v(721.25, -50.71) * mm, v(728.49, -44) * mm, v(733.9, -38.1) * mm, v(737.65, -33.23) * mm, v(739.7, -30.15) * mm, v(741.13, -27.66) * mm, v(742.1, -25.8) * mm, v(742.98, -23.92) * mm, v(744, -21.39) * mm, v(745.07, -18.17) * mm, v(746, -14.28) * mm, v(746.6, -10.42) * mm, v(746.93, -6.63) * mm, v(746.98, -3.58) * mm, v(746.91, -1.23) * mm, v(746.8, 0.47) * mm, v(746.65, 2.12) * mm, v(746.45, 3.7) * mm, v(746.22, 5.25) * mm, v(745.85, 7.32) * mm, v(745.32, 10) * mm, v(744.64, 13.49) * mm, v(743.98, 17.4) * mm, v(743.29, 23.37) * mm, v(743.08, 28.85) * mm, v(743.17, 33.15) * mm]});
            skFitSpline(sketch, "E203.trimOffspring", {"points": [v(682.58, -74.87) * mm, v(684.94, -73.19) * mm, v(689.67, -69.86) * mm, v(696.77, -64.82) * mm, v(702.74, -60.44) * mm, v(707.56, -56.76) * mm, v(711.21, -53.88) * mm, v(714.9, -50.87) * mm, v(718.56, -47.75) * mm, v(722.12, -44.54) * mm, v(725.54, -41.24) * mm, v(728.76, -37.87) * mm, v(731.73, -34.45) * mm, v(734.38, -31) * mm, v(736.28, -28.12) * mm, v(737.61, -25.84) * mm, v(738.35, -24.42) * mm, v(738.9, -23.29) * mm, v(739.4, -22.15) * mm, v(740, -20.7) * mm, v(740.61, -18.95) * mm, v(741.34, -16.6) * mm, v(742.05, -13.61) * mm, v(742.61, -10.04) * mm, v(742.91, -6.53) * mm, v(742.96, -3.7) * mm, v(742.9, -1.52) * mm, v(742.8, 0.06) * mm, v(742.66, 1.57) * mm, v(742.47, 3.03) * mm, v(742.25, 4.48) * mm, v(741.9, 6.46) * mm, v(741.38, 9.1) * mm, v(740.68, 12.65) * mm, v(740, 16.74) * mm, v(739.45, 21.42) * mm, v(739.13, 26.8) * mm, v(739.1, 30.91) * mm, v(739.15, 33.13) * mm]});
            skLineSegment(sketch, "E204", {"start": v(742.07, -13.26) * mm, "end": v(746.13, -13.26) * mm});
            skLineSegment(sketch, "E205.MirrorCS", {"start": v(627.51, -13.26) * mm, "end": v(623.44, -13.26) * mm});
            skLineSegment(sketch, "E206.MirrorCS", {"start": v(684.79, -61.42) * mm, "end": v(681.79, -61.42) * mm});
            skLineSegment(sketch, "E207.MirrorCS", {"start": v(621.43, 32) * mm, "end": v(626.43, 32) * mm});
            skLineSegment(sketch, "E208.MirrorCS", {"start": v(646.48, -87.44) * mm, "end": v(651.48, -87.44) * mm});
            skFitSpline(sketch, "E209.MirrorCS", {"points": [v(681.79, -82.2) * mm, v(652, -60.3) * mm, v(622.82, -27.7) * mm, v(618.02, 2.85) * mm, v(621.43, 32) * mm], "startDerivative": vector(-112.56, 79.93) * mm, "endDerivative": vector(-4.41, 198.36) * mm});
            skFitSpline(sketch, "E210.MirrorCS", {"points": [v(687, -74.87) * mm, v(684.63, -73.19) * mm, v(679.9, -69.86) * mm, v(672.8, -64.82) * mm, v(666.84, -60.44) * mm, v(662.01, -56.76) * mm, v(658.36, -53.88) * mm, v(654.67, -50.87) * mm, v(651.02, -47.75) * mm, v(647.45, -44.54) * mm, v(644.03, -41.24) * mm, v(640.81, -37.87) * mm, v(637.85, -34.45) * mm, v(635.2, -31) * mm, v(633.3, -28.12) * mm, v(631.97, -25.84) * mm, v(631.22, -24.42) * mm, v(630.68, -23.29) * mm, v(630.17, -22.15) * mm, v(629.59, -20.7) * mm, v(628.96, -18.95) * mm, v(628.24, -16.6) * mm, v(627.53, -13.61) * mm, v(626.97, -10.04) * mm, v(626.67, -6.53) * mm, v(626.62, -3.7) * mm, v(626.68, -1.52) * mm, v(626.78, 0.06) * mm, v(626.92, 1.57) * mm, v(627.1, 3.03) * mm, v(627.33, 4.48) * mm, v(627.68, 6.46) * mm, v(628.2, 9.1) * mm, v(628.9, 12.65) * mm, v(629.57, 16.74) * mm, v(630.12, 21.42) * mm, v(630.45, 26.8) * mm, v(630.47, 30.91) * mm, v(630.42, 33.13) * mm]});
            skLineSegment(sketch, "E211.MirrorCS", {"start": v(681.79, -61.42) * mm, "end": v(681.79, -82.2) * mm});
            skLineSegment(sketch, "E212.MirrorCS", {"start": v(684.79, -36.92) * mm, "end": v(640.01, -36.92) * mm});
            skFitSpline(sketch, "E213.MirrorCS", {"points": [v(684.66, -78.02) * mm, v(679.95, -74.68) * mm, v(672.86, -69.73) * mm, v(663.22, -62.66) * mm, v(655.86, -56.96) * mm, v(648.33, -50.71) * mm, v(641.09, -44) * mm, v(635.67, -38.1) * mm, v(631.93, -33.23) * mm, v(629.88, -30.15) * mm, v(628.44, -27.66) * mm, v(627.47, -25.8) * mm, v(626.6, -23.92) * mm, v(625.57, -21.39) * mm, v(624.51, -18.17) * mm, v(623.58, -14.28) * mm, v(622.97, -10.42) * mm, v(622.65, -6.63) * mm, v(622.6, -3.58) * mm, v(622.67, -1.23) * mm, v(622.77, 0.47) * mm, v(622.92, 2.12) * mm, v(623.12, 3.7) * mm, v(623.36, 5.25) * mm, v(623.73, 7.32) * mm, v(624.26, 10) * mm, v(624.94, 13.49) * mm, v(625.6, 17.4) * mm, v(626.3, 23.37) * mm, v(626.5, 28.85) * mm, v(626.4, 33.15) * mm]});
            skPoint(sketch, "E214", {"position": v(352.85, -197.83) * mm});
            skLineSegment(sketch, "E215.MirrorCS", {"start": v(287.7, -121.87) * mm, "end": v(283.7, -121.87) * mm});
            skLineSegment(sketch, "E216.MirrorCS", {"start": v(352.85, -174.23) * mm, "end": v(349.85, -174.23) * mm});
            skLineSegment(sketch, "E217.MirrorCS", {"start": v(288.14, -88.81) * mm, "end": v(293.14, -88.81) * mm});
            skLineSegment(sketch, "E218.MirrorCS", {"start": v(352.85, -148.23) * mm, "end": v(293.22, -148.23) * mm});
            skFitSpline(sketch, "E219.MirrorCS", {"points": [v(351.95, -192.45) * mm, v(349.68, -191.4) * mm, v(345.46, -189.71) * mm, v(339.93, -188.16) * mm, v(335.1, -187.32) * mm, v(330.93, -186.87) * mm, v(327.9, -186.56) * mm, v(325.66, -186.22) * mm, v(324.29, -185.94) * mm, v(323.18, -185.67) * mm, v(322.07, -185.35) * mm, v(320.6, -184.86) * mm, v(318.73, -184.11) * mm, v(316.8, -183.21) * mm, v(314.8, -182.17) * mm, v(312.11, -180.6) * mm, v(308.7, -178.3) * mm, v(304.69, -175.07) * mm, v(301.51, -172.04) * mm, v(299.13, -169.45) * mm, v(297.44, -167.43) * mm, v(295.87, -165.34) * mm, v(293.93, -162.48) * mm, v(291.78, -158.7) * mm, v(289.61, -153.95) * mm, v(287.83, -149.04) * mm, v(286.41, -144.09) * mm, v(285.32, -139.16) * mm, v(284.66, -135.17) * mm, v(284.27, -132.09) * mm, v(284.03, -129.84) * mm, v(283.85, -127.68) * mm, v(283.7, -124.93) * mm, v(283.65, -121.71) * mm, v(283.86, -118.11) * mm, v(284.27, -115.25) * mm, v(284.75, -112.97) * mm, v(285.2, -111.25) * mm, v(285.72, -109.52) * mm, v(286.55, -107.16) * mm, v(287.86, -104.01) * mm, v(289.6, -100.15) * mm, v(290.99, -97) * mm, v(291.94, -94.55) * mm, v(292.54, -92.73) * mm, v(292.99, -90.88) * mm, v(293.14, -89.54) * mm, v(293.14, -88.81) * mm]});
            skFitSpline(sketch, "E220.MirrorCS", {"points": [v(349.85, -196.99) * mm, v(322.14, -190.18) * mm, v(291.38, -167.23) * mm, v(279, -129.68) * mm, v(281.44, -106.62) * mm, v(288.14, -88.81) * mm], "startDerivative": vector(-203.97, 94.33) * mm, "endDerivative": vector(0, 69.3) * mm});
            skPoint(sketch, "E221.MirrorP", {"position": v(283.7, -121.87) * mm});
            skFitSpline(sketch, "E222.MirrorCS", {"points": [v(354.2, -193.36) * mm, v(352.9, -192.29) * mm, v(350.28, -190.3) * mm, v(346.26, -187.74) * mm, v(342.21, -185.51) * mm, v(338.13, -183.51) * mm, v(334.68, -181.93) * mm, v(331.87, -180.66) * mm, v(329.01, -179.37) * mm, v(325.4, -177.7) * mm, v(321.03, -175.55) * mm, v(316.72, -173.19) * mm, v(312.53, -170.57) * mm, v(308.52, -167.65) * mm, v(305.39, -164.92) * mm, v(303.03, -162.55) * mm, v(301.32, -160.63) * mm, v(299.66, -158.59) * mm, v(297.54, -155.7) * mm, v(295.08, -151.85) * mm, v(292.51, -146.95) * mm, v(290.4, -141.92) * mm, v(288.8, -136.9) * mm, v(287.94, -132.84) * mm, v(287.54, -129.76) * mm, v(287.38, -127.55) * mm, v(287.38, -125.45) * mm, v(287.5, -123.37) * mm, v(287.75, -121.3) * mm, v(288.24, -118.5) * mm, v(289.1, -114.96) * mm, v(290.25, -111.27) * mm, v(291.27, -108.2) * mm, v(292.06, -105.83) * mm, v(292.87, -103.38) * mm, v(293.66, -100.86) * mm, v(294.43, -98.25) * mm, v(295.13, -95.53) * mm, v(295.73, -92.85) * mm, v(296.41, -89.34) * mm, v(297.07, -85.12) * mm, v(297.58, -80.54) * mm, v(297.88, -76.64) * mm, v(297.96, -74.6) * mm, v(297.97, -73.72) * mm]});
            skLineSegment(sketch, "E223.MirrorCS", {"start": v(349.85, -174.23) * mm, "end": v(349.85, -196.99) * mm});
            skLineSegment(sketch, "E224", {"start": v(194.13, -69.7) * mm, "end": v(194.13, -194.17) * mm, "construction": true});
            skLineSegment(sketch, "E225", {"start": v(194.13, -170.57) * mm, "end": v(197.13, -170.57) * mm});
            skLineSegment(sketch, "E226", {"start": v(194.13, -145.57) * mm, "end": v(256.12, -145.57) * mm});
            skLineSegment(sketch, "E227", {"start": v(197.13, -170.57) * mm, "end": v(197.13, -195.12) * mm});
            skFitSpline(sketch, "E228", {"points": [v(197.13, -195.12) * mm, v(225.74, -188.44) * mm, v(255.8, -166.24) * mm, v(269.74, -130.04) * mm, v(265.53, -104.75) * mm, v(259.6, -88.78) * mm], "startDerivative": vector(203.97, 94.33) * mm, "endDerivative": vector(0, 69.3) * mm});
            skLineSegment(sketch, "E229", {"start": v(259.6, -88.78) * mm, "end": v(254.6, -88.78) * mm});
            skLineSegment(sketch, "E230", {"start": v(260.87, -122.9) * mm, "end": v(264.87, -122.9) * mm});
            skPoint(sketch, "E231", {"position": v(264.87, -122.9) * mm});
            skFitSpline(sketch, "E232.trimOffspring", {"points": [v(194.17, -192.73) * mm, v(195.47, -191.65) * mm, v(198.1, -189.66) * mm, v(202.11, -187.1) * mm, v(206.16, -184.88) * mm, v(210.24, -182.87) * mm, v(213.7, -181.3) * mm, v(216.5, -180.02) * mm, v(219.36, -178.73) * mm, v(222.98, -177.07) * mm, v(227.35, -174.91) * mm, v(231.66, -172.55) * mm, v(235.85, -169.93) * mm, v(239.85, -167) * mm, v(242.99, -164.28) * mm, v(245.34, -161.9) * mm, v(247.05, -160) * mm, v(248.71, -157.95) * mm, v(250.83, -155.07) * mm, v(253.3, -151.21) * mm, v(255.86, -146.31) * mm, v(257.97, -141.28) * mm, v(259.57, -136.26) * mm, v(260.44, -132.2) * mm, v(260.84, -129.12) * mm, v(261, -126.9) * mm, v(261, -124.81) * mm, v(260.87, -122.73) * mm, v(260.62, -120.65) * mm, v(260.14, -117.87) * mm, v(259.27, -114.32) * mm, v(258.12, -110.63) * mm, v(257.1, -107.56) * mm, v(256.31, -105.19) * mm, v(255.5, -102.75) * mm, v(254.71, -100.22) * mm, v(253.95, -97.6) * mm, v(253.24, -94.9) * mm, v(252.64, -92.21) * mm, v(251.96, -88.7) * mm, v(251.3, -84.48) * mm, v(250.8, -79.9) * mm, v(250.5, -76) * mm, v(250.42, -73.96) * mm, v(250.4, -73.08) * mm]});
            skFitSpline(sketch, "E233.trimOffspring", {"points": [v(199.9, -191.1) * mm, v(202.11, -189.94) * mm, v(206.25, -188.05) * mm, v(211.7, -186.24) * mm, v(216.48, -185.18) * mm, v(220.63, -184.53) * mm, v(223.63, -184.08) * mm, v(225.86, -183.63) * mm, v(227.22, -183.3) * mm, v(228.31, -182.97) * mm, v(229.41, -182.6) * mm, v(230.86, -182.04) * mm, v(232.68, -181.2) * mm, v(234.57, -180.21) * mm, v(236.51, -179.08) * mm, v(239.13, -177.38) * mm, v(242.43, -174.92) * mm, v(246.29, -171.5) * mm, v(249.32, -168.34) * mm, v(251.57, -165.64) * mm, v(253.16, -163.54) * mm, v(254.64, -161.38) * mm, v(256.44, -158.43) * mm, v(258.4, -154.56) * mm, v(260.35, -149.7) * mm, v(261.9, -144.72) * mm, v(263.08, -139.7) * mm, v(263.94, -134.73) * mm, v(264.41, -130.71) * mm, v(264.66, -127.61) * mm, v(264.8, -125.36) * mm, v(264.87, -123.19) * mm, v(264.9, -120.44) * mm, v(264.8, -117.22) * mm, v(264.41, -113.64) * mm, v(263.87, -110.8) * mm, v(263.28, -108.54) * mm, v(262.76, -106.85) * mm, v(262.15, -105.14) * mm, v(261.2, -102.82) * mm, v(259.75, -99.74) * mm, v(257.83, -95.96) * mm, v(256.3, -92.88) * mm, v(255.24, -90.48) * mm, v(254.55, -88.7) * mm, v(254.01, -86.86) * mm, v(253.8, -85.53) * mm, v(253.76, -84.8) * mm]});
            skPoint(sketch, "E234", {"position": v(194.13, -194.17) * mm});
            skLineSegment(sketch, "E235.MirrorCS", {"start": v(127.4, -122.9) * mm, "end": v(123.4, -122.9) * mm});
            skLineSegment(sketch, "E236.MirrorCS", {"start": v(194.13, -170.57) * mm, "end": v(191.13, -170.57) * mm});
            skLineSegment(sketch, "E237.MirrorCS", {"start": v(128.65, -88.78) * mm, "end": v(133.65, -88.78) * mm});
            skLineSegment(sketch, "E238.MirrorCS", {"start": v(194.13, -145.57) * mm, "end": v(132.14, -145.57) * mm});
            skFitSpline(sketch, "E239.MirrorCS", {"points": [v(188.36, -191.1) * mm, v(186.14, -189.94) * mm, v(182, -188.05) * mm, v(176.56, -186.24) * mm, v(171.77, -185.18) * mm, v(167.62, -184.53) * mm, v(164.62, -184.08) * mm, v(162.4, -183.63) * mm, v(161.03, -183.3) * mm, v(159.94, -182.97) * mm, v(158.84, -182.6) * mm, v(157.4, -182.04) * mm, v(155.57, -181.2) * mm, v(153.68, -180.21) * mm, v(151.74, -179.08) * mm, v(149.12, -177.38) * mm, v(145.83, -174.92) * mm, v(141.97, -171.5) * mm, v(138.94, -168.34) * mm, v(136.68, -165.64) * mm, v(135.1, -163.54) * mm, v(133.62, -161.38) * mm, v(131.82, -158.43) * mm, v(129.85, -154.56) * mm, v(127.9, -149.7) * mm, v(126.36, -144.72) * mm, v(125.17, -139.7) * mm, v(124.32, -134.73) * mm, v(123.84, -130.71) * mm, v(123.6, -127.61) * mm, v(123.46, -125.36) * mm, v(123.39, -123.19) * mm, v(123.36, -120.44) * mm, v(123.47, -117.22) * mm, v(123.84, -113.64) * mm, v(124.39, -110.8) * mm, v(124.97, -108.54) * mm, v(125.5, -106.85) * mm, v(126.1, -105.14) * mm, v(127.05, -102.82) * mm, v(128.5, -99.74) * mm, v(130.43, -95.96) * mm, v(131.96, -92.88) * mm, v(133.02, -90.48) * mm, v(133.7, -88.7) * mm, v(134.24, -86.86) * mm, v(134.46, -85.53) * mm, v(134.5, -84.8) * mm]});
            skFitSpline(sketch, "E240.MirrorCS", {"points": [v(191.13, -195.12) * mm, v(162.51, -188.44) * mm, v(132.46, -166.24) * mm, v(118.52, -130.04) * mm, v(122.72, -104.75) * mm, v(128.65, -88.78) * mm], "startDerivative": vector(-203.97, 94.33) * mm, "endDerivative": vector(0, 69.3) * mm});
            skPoint(sketch, "E241.MirrorP", {"position": v(123.4, -122.9) * mm});
            skFitSpline(sketch, "E242.MirrorCS", {"points": [v(194.1, -192.73) * mm, v(192.79, -191.65) * mm, v(190.16, -189.66) * mm, v(186.14, -187.1) * mm, v(182.1, -184.88) * mm, v(178.01, -182.87) * mm, v(174.56, -181.3) * mm, v(171.75, -180.02) * mm, v(168.9, -178.73) * mm, v(165.27, -177.07) * mm, v(160.9, -174.91) * mm, v(156.6, -172.55) * mm, v(152.4, -169.93) * mm, v(148.4, -167) * mm, v(145.27, -164.28) * mm, v(142.91, -161.9) * mm, v(141.2, -160) * mm, v(139.55, -157.95) * mm, v(137.42, -155.07) * mm, v(134.96, -151.21) * mm, v(132.4, -146.31) * mm, v(130.28, -141.28) * mm, v(128.68, -136.26) * mm, v(127.82, -132.2) * mm, v(127.42, -129.12) * mm, v(127.26, -126.9) * mm, v(127.26, -124.81) * mm, v(127.38, -122.73) * mm, v(127.63, -120.65) * mm, v(128.12, -117.87) * mm, v(128.99, -114.32) * mm, v(130.13, -110.63) * mm, v(131.15, -107.56) * mm, v(131.94, -105.19) * mm, v(132.75, -102.75) * mm, v(133.54, -100.22) * mm, v(134.31, -97.6) * mm, v(135.01, -94.9) * mm, v(135.61, -92.21) * mm, v(136.3, -88.7) * mm, v(136.95, -84.48) * mm, v(137.46, -79.9) * mm, v(137.76, -76) * mm, v(137.84, -73.96) * mm, v(137.86, -73.08) * mm]});
            skLineSegment(sketch, "E243.MirrorCS", {"start": v(191.13, -170.57) * mm, "end": v(191.13, -195.12) * mm});
            skLineSegment(sketch, "E244", {"start": v(39.7, -71.56) * mm, "end": v(39.7, -196.83) * mm, "construction": true});
            skLineSegment(sketch, "E245", {"start": v(39.7, -173.5) * mm, "end": v(42.7, -173.5) * mm});
            skLineSegment(sketch, "E246", {"start": v(39.7, -149.2) * mm, "end": v(98.83, -149.2) * mm});
            skLineSegment(sketch, "E247", {"start": v(42.7, -173.5) * mm, "end": v(42.7, -196.99) * mm});
            skFitSpline(sketch, "E248", {"points": [v(42.7, -196.99) * mm, v(73.37, -186.77) * mm, v(102.27, -161.6) * mm, v(113.54, -129.68) * mm, v(111.1, -106.62) * mm, v(105.18, -90.65) * mm], "startDerivative": vector(203.97, 94.33) * mm, "endDerivative": vector(0, 69.3) * mm});
            skLineSegment(sketch, "E249", {"start": v(105.18, -90.65) * mm, "end": v(100.18, -90.65) * mm});
            skLineSegment(sketch, "E250", {"start": v(105.16, -126.1) * mm, "end": v(109.16, -126.1) * mm});
            skPoint(sketch, "E251", {"position": v(109.16, -126.1) * mm});
            skFitSpline(sketch, "E252.trimOffspring", {"points": [v(38.34, -193.36) * mm, v(39.64, -192.29) * mm, v(42.28, -190.3) * mm, v(46.29, -187.74) * mm, v(50.34, -185.51) * mm, v(54.42, -183.51) * mm, v(57.87, -181.93) * mm, v(60.68, -180.66) * mm, v(63.54, -179.37) * mm, v(67.16, -177.7) * mm, v(71.52, -175.55) * mm, v(75.83, -173.19) * mm, v(80.02, -170.57) * mm, v(84.03, -167.65) * mm, v(87.16, -164.92) * mm, v(89.52, -162.55) * mm, v(91.23, -160.63) * mm, v(92.89, -158.59) * mm, v(95, -155.7) * mm, v(97.47, -151.85) * mm, v(100.04, -146.95) * mm, v(102.15, -141.92) * mm, v(103.75, -136.9) * mm, v(104.61, -132.84) * mm, v(105.01, -129.76) * mm, v(105.17, -127.55) * mm, v(105.17, -125.45) * mm, v(105.05, -123.37) * mm, v(104.8, -121.3) * mm, v(104.31, -118.5) * mm, v(103.44, -114.96) * mm, v(102.3, -111.27) * mm, v(101.28, -108.2) * mm, v(100.5, -105.83) * mm, v(99.68, -103.38) * mm, v(98.89, -100.86) * mm, v(98.12, -98.25) * mm, v(97.42, -95.53) * mm, v(96.82, -92.85) * mm, v(96.14, -89.34) * mm, v(95.49, -85.12) * mm, v(94.97, -80.54) * mm, v(94.67, -76.64) * mm, v(94.6, -74.6) * mm, v(94.58, -73.72) * mm]});
            skFitSpline(sketch, "E253.trimOffspring", {"points": [v(41.16, -191.41) * mm, v(43.43, -190.36) * mm, v(47.64, -188.67) * mm, v(53.17, -187.1) * mm, v(58, -186.25) * mm, v(62.17, -185.8) * mm, v(65.2, -185.49) * mm, v(67.44, -185.14) * mm, v(68.81, -184.86) * mm, v(69.92, -184.59) * mm, v(71.03, -184.27) * mm, v(72.5, -183.77) * mm, v(74.36, -183.02) * mm, v(76.3, -182.12) * mm, v(78.28, -181.07) * mm, v(80.98, -179.49) * mm, v(84.38, -177.18) * mm, v(88.4, -173.95) * mm, v(91.57, -170.92) * mm, v(93.94, -168.33) * mm, v(95.62, -166.3) * mm, v(97.2, -164.21) * mm, v(99.13, -161.35) * mm, v(101.27, -157.57) * mm, v(103.43, -152.8) * mm, v(105.2, -147.9) * mm, v(106.61, -142.94) * mm, v(107.7, -138.01) * mm, v(108.35, -134.02) * mm, v(108.74, -130.94) * mm, v(108.97, -128.69) * mm, v(109.14, -126.52) * mm, v(109.3, -123.78) * mm, v(109.34, -120.56) * mm, v(109.12, -116.96) * mm, v(108.7, -114.1) * mm, v(108.22, -111.82) * mm, v(107.78, -110.1) * mm, v(107.25, -108.37) * mm, v(106.41, -106.02) * mm, v(105.1, -102.87) * mm, v(103.35, -99) * mm, v(101.96, -95.86) * mm, v(101, -93.41) * mm, v(100.4, -91.6) * mm, v(99.95, -89.74) * mm, v(99.8, -88.4) * mm, v(99.8, -87.68) * mm]});
            skLineSegment(sketch, "E254.MirrorCS", {"start": v(-25.77, -126.1) * mm, "end": v(-29.77, -126.1) * mm});
            skLineSegment(sketch, "E255.MirrorCS", {"start": v(39.7, -173.5) * mm, "end": v(36.7, -173.5) * mm});
            skLineSegment(sketch, "E256.MirrorCS", {"start": v(-25.78, -90.65) * mm, "end": v(-20.78, -90.65) * mm});
            skLineSegment(sketch, "E257.MirrorCS", {"start": v(39.7, -149.2) * mm, "end": v(-19.43, -149.2) * mm});
            skFitSpline(sketch, "E258.MirrorCS", {"points": [v(38.24, -191.41) * mm, v(35.97, -190.36) * mm, v(31.75, -188.67) * mm, v(26.23, -187.1) * mm, v(21.4, -186.25) * mm, v(17.22, -185.8) * mm, v(14.2, -185.49) * mm, v(11.96, -185.14) * mm, v(10.59, -184.86) * mm, v(9.48, -184.59) * mm, v(8.37, -184.27) * mm, v(6.9, -183.77) * mm, v(5.03, -183.02) * mm, v(3.1, -182.12) * mm, v(1.11, -181.07) * mm, v(-1.58, -179.49) * mm, v(-4.99, -177.18) * mm, v(-9, -173.95) * mm, v(-12.17, -170.92) * mm, v(-14.54, -168.33) * mm, v(-16.22, -166.3) * mm, v(-17.8, -164.21) * mm, v(-19.73, -161.35) * mm, v(-21.87, -157.57) * mm, v(-24.03, -152.8) * mm, v(-25.8, -147.9) * mm, v(-27.21, -142.94) * mm, v(-28.3, -138.01) * mm, v(-28.95, -134.02) * mm, v(-29.34, -130.94) * mm, v(-29.57, -128.69) * mm, v(-29.75, -126.52) * mm, v(-29.9, -123.78) * mm, v(-29.94, -120.56) * mm, v(-29.72, -116.96) * mm, v(-29.31, -114.1) * mm, v(-28.83, -111.82) * mm, v(-28.38, -110.1) * mm, v(-27.85, -108.37) * mm, v(-27.01, -106.02) * mm, v(-25.7, -102.87) * mm, v(-23.95, -99) * mm, v(-22.56, -95.86) * mm, v(-21.6, -93.41) * mm, v(-21, -91.6) * mm, v(-20.55, -89.74) * mm, v(-20.4, -88.4) * mm, v(-20.4, -87.68) * mm]});
            skFitSpline(sketch, "E259.MirrorCS", {"points": [v(36.7, -196.99) * mm, v(6.02, -186.77) * mm, v(-22.87, -161.6) * mm, v(-34.15, -129.68) * mm, v(-31.7, -106.62) * mm, v(-25.78, -90.65) * mm], "startDerivative": vector(-203.97, 94.33) * mm, "endDerivative": vector(0, 69.3) * mm});
            skPoint(sketch, "E260.MirrorP", {"position": v(-29.77, -126.1) * mm});
            skFitSpline(sketch, "E261.MirrorCS", {"points": [v(41.06, -193.36) * mm, v(39.76, -192.29) * mm, v(37.12, -190.3) * mm, v(33.11, -187.74) * mm, v(29.06, -185.51) * mm, v(24.98, -183.51) * mm, v(21.53, -181.93) * mm, v(18.71, -180.66) * mm, v(15.86, -179.37) * mm, v(12.24, -177.7) * mm, v(7.87, -175.55) * mm, v(3.56, -173.19) * mm, v(-0.63, -170.57) * mm, v(-4.63, -167.65) * mm, v(-7.76, -164.92) * mm, v(-10.12, -162.55) * mm, v(-11.83, -160.63) * mm, v(-13.49, -158.59) * mm, v(-15.61, -155.7) * mm, v(-18.07, -151.85) * mm, v(-20.64, -146.95) * mm, v(-22.75, -141.92) * mm, v(-24.35, -136.9) * mm, v(-25.22, -132.84) * mm, v(-25.62, -129.76) * mm, v(-25.77, -127.55) * mm, v(-25.78, -125.45) * mm, v(-25.65, -123.37) * mm, v(-25.4, -121.3) * mm, v(-24.91, -118.5) * mm, v(-24.04, -114.96) * mm, v(-22.9, -111.27) * mm, v(-21.89, -108.2) * mm, v(-21.1, -105.83) * mm, v(-20.29, -103.38) * mm, v(-19.49, -100.86) * mm, v(-18.72, -98.25) * mm, v(-18.02, -95.53) * mm, v(-17.42, -92.85) * mm, v(-16.74, -89.34) * mm, v(-16.09, -85.12) * mm, v(-15.57, -80.54) * mm, v(-15.27, -76.64) * mm, v(-15.2, -74.6) * mm, v(-15.18, -73.72) * mm]});
            skLineSegment(sketch, "E262.MirrorCS", {"start": v(36.7, -173.5) * mm, "end": v(36.7, -196.99) * mm});
            skLineSegment(sketch, "E263", {"start": v(-111.24, -69.7) * mm, "end": v(-111.24, -194.96) * mm, "construction": true});
            skLineSegment(sketch, "E264", {"start": v(-111.24, -172.6) * mm, "end": v(-108.24, -172.6) * mm});
            skLineSegment(sketch, "E265", {"start": v(-111.24, -148.6) * mm, "end": v(-56.95, -148.6) * mm});
            skLineSegment(sketch, "E266", {"start": v(-108.24, -172.6) * mm, "end": v(-108.24, -195.12) * mm});
            skFitSpline(sketch, "E267", {"points": [v(-108.24, -195.12) * mm, v(-77.72, -181.16) * mm, v(-55.49, -161.1) * mm, v(-39.06, -118.63) * mm, v(-45.76, -88.78) * mm], "startDerivative": vector(203.97, 94.33) * mm, "endDerivative": vector(0, 69.3) * mm});
            skLineSegment(sketch, "E268", {"start": v(-45.76, -88.78) * mm, "end": v(-50.76, -88.78) * mm});
            skLineSegment(sketch, "E269", {"start": v(-48.49, -125.55) * mm, "end": v(-44.49, -125.55) * mm});
            skPoint(sketch, "E270", {"position": v(-44.49, -125.55) * mm});
            skFitSpline(sketch, "E271.trimOffspring", {"points": [v(-115.08, -188.6) * mm, v(-113.78, -187.52) * mm, v(-111.14, -185.53) * mm, v(-107.13, -182.97) * mm, v(-103.08, -180.75) * mm, v(-99, -178.74) * mm, v(-95.55, -177.16) * mm, v(-92.73, -175.9) * mm, v(-89.88, -174.6) * mm, v(-86.26, -172.94) * mm, v(-81.9, -170.78) * mm, v(-77.58, -168.42) * mm, v(-73.4, -165.8) * mm, v(-69.4, -162.88) * mm, v(-66.26, -160.15) * mm, v(-63.9, -157.78) * mm, v(-62.2, -155.87) * mm, v(-60.53, -153.82) * mm, v(-58.4, -150.94) * mm, v(-55.95, -147.08) * mm, v(-53.38, -142.18) * mm, v(-51.27, -137.15) * mm, v(-49.67, -132.13) * mm, v(-48.8, -128.08) * mm, v(-48.4, -125) * mm, v(-48.25, -122.78) * mm, v(-48.24, -120.68) * mm, v(-48.37, -118.6) * mm, v(-48.62, -116.53) * mm, v(-49.1, -113.74) * mm, v(-49.98, -110.2) * mm, v(-51.12, -106.5) * mm, v(-52.13, -103.43) * mm, v(-52.93, -101.06) * mm, v(-53.73, -98.62) * mm, v(-54.53, -96.1) * mm, v(-55.3, -93.48) * mm, v(-56, -90.77) * mm, v(-56.6, -88.08) * mm, v(-57.28, -84.57) * mm, v(-57.93, -80.35) * mm, v(-58.45, -75.78) * mm, v(-58.75, -71.87) * mm, v(-58.83, -69.83) * mm, v(-58.84, -68.95) * mm]});
            skLineSegment(sketch, "E272.MirrorCS", {"start": v(-174, -125.55) * mm, "end": v(-178, -125.55) * mm});
            skLineSegment(sketch, "E273.MirrorCS", {"start": v(-111.24, -172.6) * mm, "end": v(-114.24, -172.6) * mm});
            skLineSegment(sketch, "E274.MirrorCS", {"start": v(-176.72, -88.78) * mm, "end": v(-171.72, -88.78) * mm});
            skLineSegment(sketch, "E275.MirrorCS", {"start": v(-111.24, -148.6) * mm, "end": v(-165.52, -148.6) * mm});
            skFitSpline(sketch, "E276.MirrorCS", {"points": [v(-114.24, -195.12) * mm, v(-144.76, -181.16) * mm, v(-166.99, -161.1) * mm, v(-183.41, -118.63) * mm, v(-176.72, -88.78) * mm], "startDerivative": vector(-203.97, 94.33) * mm, "endDerivative": vector(0, 69.3) * mm});
            skPoint(sketch, "E277.MirrorP", {"position": v(-178, -125.55) * mm});
            skFitSpline(sketch, "E278.MirrorCS", {"points": [v(-107.4, -188.6) * mm, v(-108.7, -187.52) * mm, v(-111.34, -185.53) * mm, v(-115.35, -182.97) * mm, v(-119.4, -180.75) * mm, v(-123.48, -178.74) * mm, v(-126.93, -177.16) * mm, v(-129.74, -175.9) * mm, v(-132.6, -174.6) * mm, v(-136.22, -172.94) * mm, v(-140.58, -170.78) * mm, v(-144.9, -168.42) * mm, v(-149.08, -165.8) * mm, v(-153.09, -162.88) * mm, v(-156.22, -160.15) * mm, v(-158.58, -157.78) * mm, v(-160.29, -155.87) * mm, v(-161.95, -153.82) * mm, v(-164.07, -150.94) * mm, v(-166.53, -147.08) * mm, v(-169.1, -142.18) * mm, v(-171.2, -137.15) * mm, v(-172.8, -132.13) * mm, v(-173.67, -128.08) * mm, v(-174.07, -125) * mm, v(-174.23, -122.78) * mm, v(-174.23, -120.68) * mm, v(-174.1, -118.6) * mm, v(-173.86, -116.53) * mm, v(-173.37, -113.74) * mm, v(-172.5, -110.2) * mm, v(-171.36, -106.5) * mm, v(-170.34, -103.43) * mm, v(-169.55, -101.06) * mm, v(-168.74, -98.62) * mm, v(-167.95, -96.1) * mm, v(-167.18, -93.48) * mm, v(-166.48, -90.77) * mm, v(-165.88, -88.08) * mm, v(-165.2, -84.57) * mm, v(-164.55, -80.35) * mm, v(-164.03, -75.78) * mm, v(-163.73, -71.87) * mm, v(-163.65, -69.83) * mm, v(-163.64, -68.95) * mm]});
            skLineSegment(sketch, "E279.MirrorCS", {"start": v(-114.24, -172.6) * mm, "end": v(-114.24, -195.12) * mm});
            skFitSpline(sketch, "E280", {"points": [v(-44.49, -125.55) * mm, v(-50.76, -88.78) * mm], "startDerivative": vector(5.5, 38.92) * mm, "endDerivative": vector(-6.27, 36.77) * mm});
            skFitSpline(sketch, "E281.MirrorCS", {"points": [v(-178, -125.55) * mm, v(-171.72, -88.78) * mm], "startDerivative": vector(-5.5, 38.92) * mm, "endDerivative": vector(6.27, 36.77) * mm});
            skSolve(sketch);
        }
        {
            var Q0;
            Q0=qCreatedBy(makeId("Front.planeOp"),FACE);
            var sketch = newSketch(context, id + "F1", { "sketchPlane" : qUnion([Q0])});
            skLineSegment(sketch, "E282", {"start": v(-52.76, 27.43) * mm, "end": v(-66.2, 28.76) * mm});
            skLineSegment(sketch, "E283", {"start": v(11.17, 21.07) * mm, "end": v(11.17, -8.93) * mm});
            skFitSpline(sketch, "E284", {"points": [v(11.17, -8.93) * mm, v(433.17, -23.97) * mm], "startDerivative": vector(483.4, -44.47) * mm, "endDerivative": vector(364.06, -0.9) * mm});
            skLineSegment(sketch, "E285", {"start": v(433.17, -23.97) * mm, "end": v(433.17, 6.03) * mm});
            skLineSegment(sketch, "E286", {"start": v(433.17, 6.03) * mm, "end": v(447.96, 6.03) * mm});
            skLineSegment(sketch, "E287", {"start": v(-44.4, -71.24) * mm, "end": v(-66.2, 28.76) * mm});
            skLineSegment(sketch, "E288", {"start": v(-52.76, 6.4) * mm, "end": v(-46.76, 6.4) * mm});
            skFitSpline(sketch, "E289", {"points": [v(472.46, 6.03) * mm, v(406.44, -71.25) * mm], "startDerivative": vector(-9.53, -105.37) * mm, "endDerivative": vector(-148.23, -30.56) * mm});
            skLineSegment(sketch, "E290", {"start": v(-44.4, -71.24) * mm, "end": v(406.44, -71.25) * mm});
            skLineSegment(sketch, "E291", {"start": v(-39.83, 26.14) * mm, "end": v(-39.83, -3.87) * mm});
            skLineSegment(sketch, "E292", {"start": v(-39.83, -3.87) * mm, "end": v(-33.83, -3.87) * mm});
            skLineSegment(sketch, "E293", {"start": v(-33.83, -3.87) * mm, "end": v(-33.83, 25.54) * mm});
            skLineSegment(sketch, "E294", {"start": v(-66.2, 28.76) * mm, "end": v(474.62, 28.76) * mm, "construction": true});
            skLineSegment(sketch, "E295", {"start": v(474.62, 28.76) * mm, "end": v(474.62, -71.73) * mm, "construction": true});
            skLineSegment(sketch, "E296", {"start": v(-66.2, -70.56) * mm, "end": v(-66.2, 28.76) * mm, "construction": true});
            skLineSegment(sketch, "E297.trimOffspring", {"start": v(-13.78, 23.55) * mm, "end": v(-33.83, 25.54) * mm});
            skLineSegment(sketch, "E298", {"start": v(-46.76, 6.4) * mm, "end": v(-46.76, 26.83) * mm});
            skLineSegment(sketch, "E299", {"start": v(-52.76, 6.4) * mm, "end": v(-52.76, 27.43) * mm});
            skLineSegment(sketch, "E300.trimOffspring", {"start": v(-39.83, 26.14) * mm, "end": v(-46.76, 26.83) * mm});
            skLineSegment(sketch, "E301", {"start": v(447.96, -20.87) * mm, "end": v(453.96, -20.87) * mm});
            skLineSegment(sketch, "E302", {"start": v(453.96, -20.87) * mm, "end": v(453.96, 6.03) * mm});
            skLineSegment(sketch, "E303", {"start": v(447.96, -20.87) * mm, "end": v(447.96, 6.03) * mm});
            skLineSegment(sketch, "E304.trimOffspring", {"start": v(453.96, 6.03) * mm, "end": v(472.46, 6.03) * mm});
            skLineSegment(sketch, "E305", {"start": v(427.17, -23.97) * mm, "end": v(427.17, -44.5) * mm});
            skLineSegment(sketch, "E306", {"start": v(427.17, -44.5) * mm, "end": v(421.17, -44.5) * mm});
            skLineSegment(sketch, "E307", {"start": v(421.17, -44.5) * mm, "end": v(421.17, -30.88) * mm});
            skLineSegment(sketch, "E308", {"start": v(-13.78, 23.55) * mm, "end": v(-13.78, -15.2) * mm});
            skLineSegment(sketch, "E309", {"start": v(-13.78, -15.2) * mm, "end": v(-7.78, -15.2) * mm});
            skLineSegment(sketch, "E310", {"start": v(-7.78, -15.2) * mm, "end": v(-7.78, 22.95) * mm});
            skLineSegment(sketch, "E311.trimOffspring", {"start": v(11.17, 21.07) * mm, "end": v(-7.78, 22.95) * mm});
            skLineSegment(sketch, "E312", {"start": v(421.17, -30.88) * mm, "end": v(399.17, -30.88) * mm});
            skLineSegment(sketch, "E313", {"start": v(399.17, -30.88) * mm, "end": v(399.17, -23.88) * mm});
            skLineSegment(sketch, "E314", {"start": v(389.84, -23.86) * mm, "end": v(389.84, -48.36) * mm});
            skLineSegment(sketch, "E315", {"start": v(389.84, -48.36) * mm, "end": v(383.84, -48.36) * mm});
            skLineSegment(sketch, "E316", {"start": v(383.84, -48.36) * mm, "end": v(383.84, -23.83) * mm});
            skLineSegment(sketch, "E317", {"start": v(23.77, -10.06) * mm, "end": v(23.77, -39.06) * mm});
            skLineSegment(sketch, "E318", {"start": v(23.77, -39.06) * mm, "end": v(29.77, -39.06) * mm});
            skLineSegment(sketch, "E319", {"start": v(29.77, -39.06) * mm, "end": v(29.77, -10.59) * mm});
            skLineSegment(sketch, "E320", {"start": v(62.99, -13.26) * mm, "end": v(62.99, -42.26) * mm});
            skLineSegment(sketch, "E321", {"start": v(62.99, -42.26) * mm, "end": v(68.99, -42.26) * mm});
            skLineSegment(sketch, "E322", {"start": v(68.99, -42.26) * mm, "end": v(68.99, -13.7) * mm});
            skLineSegment(sketch, "E323", {"start": v(100.73, -15.5) * mm, "end": v(100.73, -44.5) * mm});
            skLineSegment(sketch, "E324", {"start": v(100.73, -44.5) * mm, "end": v(106.73, -44.5) * mm});
            skLineSegment(sketch, "E325", {"start": v(106.73, -44.5) * mm, "end": v(106.73, -15.8) * mm});
            skLineSegment(sketch, "E326", {"start": v(139.7, -18.12) * mm, "end": v(139.7, -46.12) * mm});
            skLineSegment(sketch, "E327", {"start": v(139.7, -46.12) * mm, "end": v(145.7, -46.12) * mm});
            skLineSegment(sketch, "E328", {"start": v(145.7, -46.12) * mm, "end": v(145.7, -18.43) * mm});
            skLineSegment(sketch, "E329", {"start": v(154.38, -18.85) * mm, "end": v(154.38, -25.85) * mm});
            skLineSegment(sketch, "E330", {"start": v(183.72, -20.13) * mm, "end": v(183.72, -46.13) * mm});
            skLineSegment(sketch, "E331", {"start": v(183.72, -46.13) * mm, "end": v(177.72, -46.13) * mm});
            skLineSegment(sketch, "E332", {"start": v(177.72, -46.13) * mm, "end": v(177.72, -25.85) * mm});
            skLineSegment(sketch, "E333", {"start": v(154.38, -25.85) * mm, "end": v(177.72, -25.85) * mm});
            skLineSegment(sketch, "E334", {"start": v(223.07, -21.5) * mm, "end": v(223.07, -47.68) * mm});
            skLineSegment(sketch, "E335", {"start": v(223.07, -47.68) * mm, "end": v(229.07, -47.68) * mm});
            skLineSegment(sketch, "E336", {"start": v(229.07, -47.68) * mm, "end": v(229.07, -21.68) * mm});
            skLineSegment(sketch, "E337", {"start": v(268.66, -22.63) * mm, "end": v(268.66, -47.68) * mm});
            skLineSegment(sketch, "E338", {"start": v(268.66, -47.68) * mm, "end": v(274.66, -47.74) * mm});
            skLineSegment(sketch, "E339", {"start": v(274.66, -47.74) * mm, "end": v(274.66, -22.74) * mm});
            skLineSegment(sketch, "E340", {"start": v(427.17, -23.97) * mm, "end": v(433.17, -23.97) * mm});
            skLineSegment(sketch, "E341", {"start": v(307.12, -23.25) * mm, "end": v(307.12, -47.68) * mm});
            skLineSegment(sketch, "E342", {"start": v(307.12, -47.68) * mm, "end": v(313.12, -47.68) * mm});
            skLineSegment(sketch, "E343", {"start": v(313.12, -47.68) * mm, "end": v(313.12, -23.32) * mm});
            skLineSegment(sketch, "E344", {"start": v(344.77, -23.62) * mm, "end": v(344.77, -47.68) * mm});
            skLineSegment(sketch, "E345", {"start": v(344.77, -47.68) * mm, "end": v(350.77, -47.68) * mm});
            skLineSegment(sketch, "E346", {"start": v(350.77, -47.68) * mm, "end": v(350.77, -23.67) * mm});
            skSolve(sketch);
        }
        {
            var Q0;
            Q0 = qSketchRegion(id + "F1", true);
            extrude(context, id + "F2", {"entities" : qUnion([Q0]), "depth" : 6 * mm, "offsetDistance" : 25 * mm});
        }
        {
            var Q0;
            Q0=makeQuery(id+"F0.imprint","IMPRINT",FACE,{"disambiguationData":[TD([[makeQuery(id+"F0.imprint","IMPRINT",EDGE,{"derivedFrom":sQuery(id+"F0.wireOp",EDGE,"E2")}),-1.0]])]});
            extrude(context, id + "F3", {"entities" : qUnion([Q0]), "depth" : 6 * mm, "offsetDistance" : 25 * mm});
        }
        {
            var Q0;
            Q0 = qSketchRegion(id + "F0", true);
            extrude(context, id + "F4", {"entities" : qUnion([Q0]), "operationType" : NewBodyOperationType.ADD, "depth" : 6 * mm, "offsetDistance" : 25 * mm});
        }
    });
